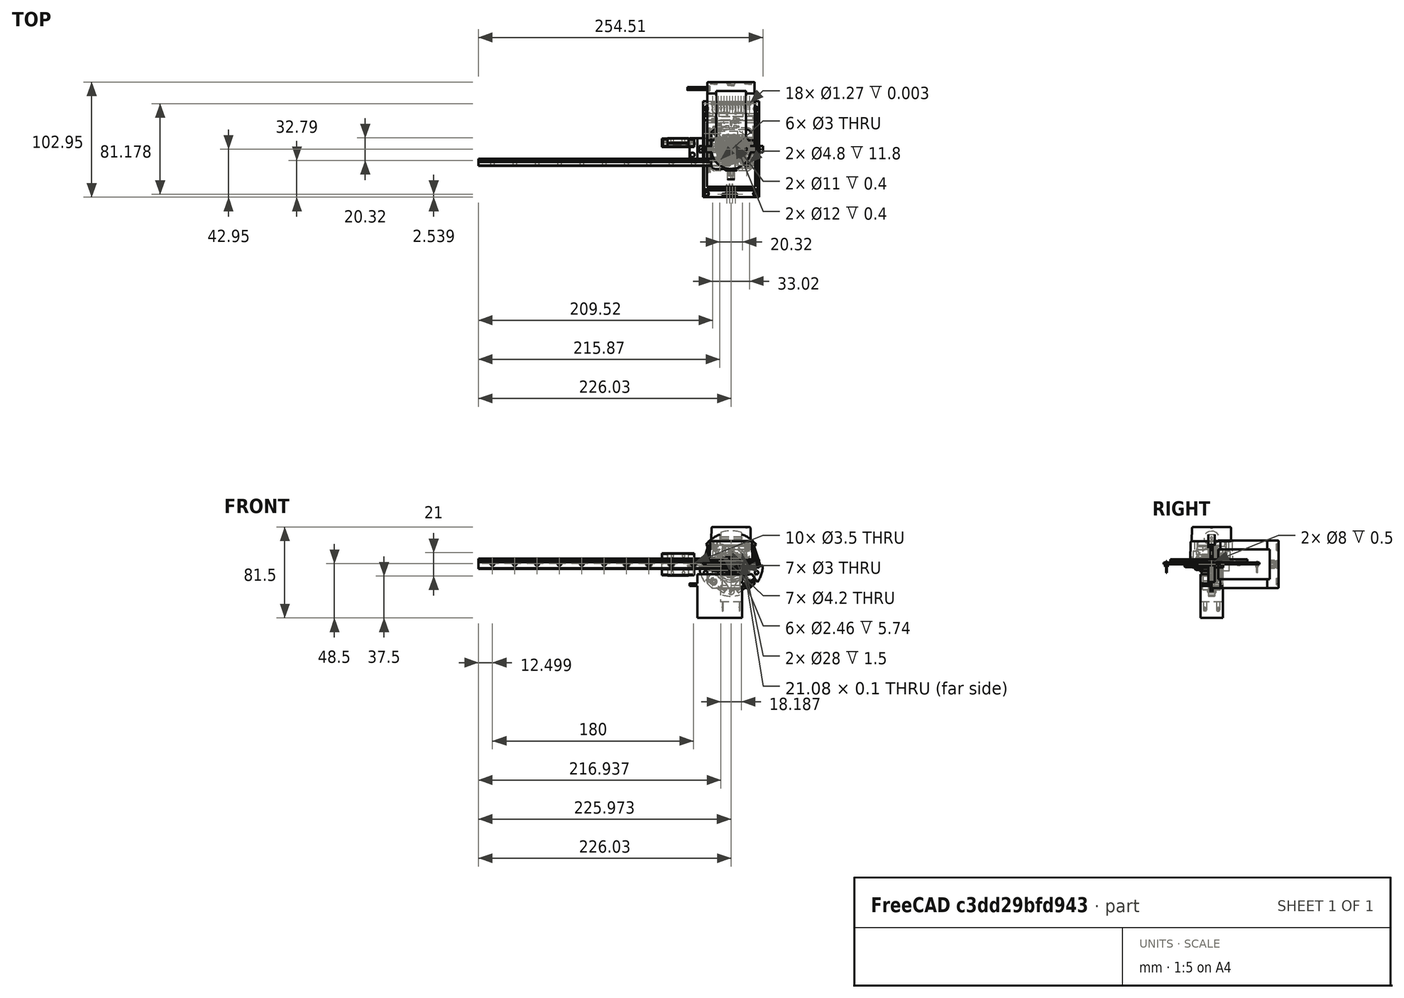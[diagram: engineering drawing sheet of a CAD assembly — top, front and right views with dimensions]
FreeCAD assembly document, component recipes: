
FREECAD ASSEMBLY — COMPONENT RECIPES ("generic-hardware")

This assembly document has 34 components, labeled P0..P33 below (a component is one placed body or linked part). 32 of them carry a construction recipe — the FreeCAD feature program that regenerates the part from scratch, quoted from this document or its linked companion documents; the rest are supplied as boundary geometry only. No exploded tour is included for this assembly.
NOTE — document 2 of 3 of this assembly tour. The two overview renders and the header above are repeated from document 1; the component sections below continue where the previous document stopped.
COMPONENT P17 — recipe-attached ("LD06", modeled in this document).
Construction recipe (the document's own serialized feature program — sketch geometry with constraints, then the solid features built on it; lengths are millimeters unless a unit is written):

FEATURE [Sketcher::SketchObject] Sketch189
  ArcFitTolerance = 0
  ExternalBSplineMaxDegree = 0
  ExternalBSplineTolerance = 0
  FixShape = 1
  FullyConstrained = true
  InternalTolerance = 1e-06
  InvalidShape = false
  MakeInternals = false
  MapMode = 5
  TreeRank = 0
  ValidateShape = false
  sketch-geometry (10):
    g0: ArcOfCircle CenterX=-14.1 CenterY=14.1 CenterZ=0 NormalX=0 NormalY=0 NormalZ=1 AngleXU=0 Radius=5.195 StartAngle=1.5708 EndAngle=3.14159
    g1: LineSegment StartX=-14.1 StartY=19.295 StartZ=0 EndX=14.1 EndY=19.295 EndZ=0
    g2: ArcOfCircle CenterX=14.1 CenterY=14.1 CenterZ=0 NormalX=0 NormalY=0 NormalZ=1 AngleXU=0 Radius=5.195 StartAngle=6.5809e-12 EndAngle=1.5708
    g3: LineSegment StartX=19.295 StartY=14.1 StartZ=0 EndX=19.295 EndY=-14.1 EndZ=0
    g4: ArcOfCircle CenterX=14.1 CenterY=-14.1 CenterZ=0 NormalX=0 NormalY=0 NormalZ=1 AngleXU=0 Radius=5.195 StartAngle=4.71239 EndAngle=6.28319
    g5: LineSegment StartX=14.1 StartY=-19.295 StartZ=0 EndX=-14.1 EndY=-19.295 EndZ=0
    g6: ArcOfCircle CenterX=-14.1 CenterY=-14.1 CenterZ=0 NormalX=0 NormalY=0 NormalZ=1 AngleXU=0 Radius=5.195 StartAngle=3.14159 EndAngle=4.71239
    g7: LineSegment StartX=-19.295 StartY=-14.1 StartZ=0 EndX=-19.295 EndY=14.1 EndZ=0
    g8: GeomPoint [constr] X=-19.295 Y=19.295 Z=0
    g9: GeomPoint [constr] X=19.295 Y=-19.295 Z=0
  constraints (23):
    c: Tangent(g0,g1) = 1.5708
    c: Tangent(g1,g2) = 1.5708
    c: Tangent(g2,g3) = 1.5708
    c: Tangent(g3,g4) = 1.5708
    c: Tangent(g4,g5) = 1.5708
    c: Tangent(g5,g6) = 1.5708
    c: Tangent(g6,g7) = 1.5708
    c: Tangent(g7,g0) = 1.5708
    c: Horizontal(g1)
    c: Horizontal(g5)
    c: Vertical(g3)
    c: Vertical(g7)
    c: Equal(g0,g2)
    c: Equal(g2,g4)
    c: Equal(g4,g6)
    c: PointOnObject(g8,g1)
    c: PointOnObject(g8,g7)
    c: PointOnObject(g9,g3)
    c: PointOnObject(g9,g5)
    c: Symmetric(g0,g4,g-1)
    c: Equal(g1,g3)
    c: DistanceY(g4,g1) = 38.59
    c: DistanceX(g0,g2) = 28.2
FEATURE [PartDesign::Pad] Pad077
  AddSubType = 0
  AlongSketchNormal = false
  AutoTaperInnerAngle = true
  CheckUpToFaceLimits = true
  ClaimChildren = false
  Direction = (0,0,1)
  Fit = 0
  FitJoin = 0
  FixShape = 1
  InnerFit = 0
  InnerFitJoin = 0
  InvalidShape = false
  Length = 20.7
  Length2 = 100
  NewSolid = false
  Profile = -> Sketch189
  Refine = true
  Suppress = false
  TaperAngle = -2
  TaperInnerAngle = 2
  TaperInnerAngleRev = 0
  TreeRank = 0
  Type = 0
  ValidateShape = true
  _ProfileBasedVersion = 0
FEATURE [Sketcher::SketchObject] Sketch190
  ArcFitTolerance = 0
  AttachmentSupport = -> [Pad077]
  ExternalBSplineMaxDegree = 0
  ExternalBSplineTolerance = 0
  FixShape = 1
  FullyConstrained = true
  InternalTolerance = 1e-06
  InvalidShape = false
  MakeInternals = false
  MapMode = 5
  Placement = pos=(0,0,20.7) rot=(0,0,1;0rad)
  Support = -> [Pad077]
  TreeRank = 0
  ValidateShape = false
  sketch-geometry (1):
    g0: Circle CenterX=0 CenterY=0 CenterZ=0 NormalX=0 NormalY=0 NormalZ=1 AngleXU=0 Radius=17.645
  constraints (2):
    c: Coincident(g0,g-1)
    c: Diameter(g0) = 35.29
FEATURE [PartDesign::Pad] Pad078
  AddSubType = 0
  AlongSketchNormal = false
  AutoTaperInnerAngle = true
  BaseFeature = -> Pad077
  CheckUpToFaceLimits = true
  ClaimChildren = false
  Direction = (0,0,1)
  Fit = 0
  FitJoin = 0
  FixShape = 1
  InnerFit = 0
  InnerFitJoin = 0
  InvalidShape = false
  Length = 12.8
  Length2 = 100
  NewSolid = false
  Profile = -> Sketch190
  Refine = true
  Suppress = false
  TaperAngle = -1.5
  TaperInnerAngle = 1.5
  TaperInnerAngleRev = 0
  TreeRank = 0
  Type = 0
  ValidateShape = true
  _ProfileBasedVersion = 0
FEATURE [Sketcher::SketchObject] Sketch191
  ArcFitTolerance = 0
  AttachmentOffset = pos=(0,0,17) rot=(0,0,1;0rad)
  ExternalBSplineMaxDegree = 0
  ExternalBSplineTolerance = 0
  FixShape = 1
  FullyConstrained = true
  InternalTolerance = 1e-06
  InvalidShape = false
  MakeInternals = false
  MapMode = 5
  Placement = pos=(0,-17,-4e-15) rot=(1,0,0;1.5708rad)
  TreeRank = 0
  ValidateShape = false
  sketch-geometry (5):
    g0: LineSegment StartX=-5 StartY=6.3 StartZ=0 EndX=-5 EndY=1.3 EndZ=0
    g1: LineSegment StartX=-5 StartY=1.3 StartZ=0 EndX=5 EndY=1.3 EndZ=0
    g2: LineSegment StartX=5 StartY=1.3 StartZ=0 EndX=5 EndY=6.3 EndZ=0
    g3: LineSegment StartX=5 StartY=6.3 StartZ=0 EndX=-5 EndY=6.3 EndZ=0
    g4: GeomPoint [constr] X=1.3758e-12 Y=3.8 Z=0
  constraints (13):
    c: Coincident(g0,g1)
    c: Coincident(g1,g2)
    c: Coincident(g2,g3)
    c: Coincident(g3,g0)
    c: Horizontal(g1)
    c: Horizontal(g3)
    c: Vertical(g0)
    c: Vertical(g2)
    c: Symmetric(g1,g0,g4)
    c: PointOnObject(g4,g-2)
    c: DistanceX(g3,g3) = 10
    c: DistanceY(g2,g2) = 5
    c: DistanceY(g-1,g4) = 3.8
FEATURE [PartDesign::Pocket] Pocket061
  AddSubType = 1
  AutoTaperInnerAngle = true
  BaseFeature = -> Pad078
  CheckUpToFaceLimits = true
  ClaimChildren = false
  Direction = (0,1,0)
  Fit = 0
  FitJoin = 0
  FixShape = 1
  InnerFit = 0
  InnerFitJoin = 0
  InvalidShape = false
  Length = 5
  Length2 = 100
  NewSolid = false
  Profile = -> Sketch191
  Refine = true
  Reversed = true
  Suppress = false
  TaperInnerAngle = 0
  TaperInnerAngleRev = 0
  TreeRank = 0
  Type = 1
  ValidateShape = true
  _ProfileBasedVersion = 0
  _Version = 0
FEATURE [Sketcher::SketchObject] Sketch192
  ArcFitTolerance = 0
  AttachmentSupport = -> [Pocket061]
  ExternalBSplineMaxDegree = 0
  ExternalBSplineTolerance = 0
  FixShape = 1
  FullyConstrained = false
  InternalTolerance = 1e-06
  InvalidShape = false
  MakeInternals = false
  MapMode = 5
  Placement = pos=(0,-17,0) rot=(1,0,0;1.5708rad)
  Support = -> [Pocket061]
  TreeRank = 0
  ValidateShape = false
  sketch-geometry (8):
    g0: Circle CenterX=-2.295 CenterY=3.8 CenterZ=0 NormalX=0 NormalY=0 NormalZ=1 AngleXU=0 Radius=0.765
    g1: Circle CenterX=-0.765 CenterY=3.8 CenterZ=0 NormalX=0 NormalY=0 NormalZ=1 AngleXU=0 Radius=0.765
    g2: Circle CenterX=0.765 CenterY=3.8 CenterZ=0 NormalX=0 NormalY=0 NormalZ=1 AngleXU=0 Radius=0.765
    g3: Circle CenterX=2.295 CenterY=3.8 CenterZ=0 NormalX=0 NormalY=0 NormalZ=1 AngleXU=0 Radius=0.765
    g4: LineSegment [constr] StartX=-2.295 StartY=3.8 StartZ=0 EndX=-0.765 EndY=3.8 EndZ=0
    g5: LineSegment [constr] StartX=-0.765 StartY=3.8 StartZ=0 EndX=0.765 EndY=3.8 EndZ=0
    g6: LineSegment [constr] StartX=0.765 StartY=3.8 StartZ=0 EndX=2.295 EndY=3.8 EndZ=0
    g7: GeomPoint [constr] X=1.8986e-12 Y=3.8 Z=0
  constraints (16):
    c: Horizontal(g3,g2)
    c: Symmetric(g1,g2,g-2)
    c: Symmetric(g0,g3,g-2)
    c: Coincident(g4,g0)
    c: Coincident(g4,g1)
    c: Coincident(g5,g1)
    c: Coincident(g5,g2)
    c: Coincident(g6,g2)
    c: Coincident(g6,g3)
    c: Equal(g6,g5)
    c: PointOnObject(g7,g5)
    c: Equal(g0,g1)
    c: Equal(g1,g2)
    c: Equal(g2,g3)
    c: Tangent(g3,g2)
    c: DistanceX(g4,g4) = 1.53
FEATURE [PartDesign::Pad] Pad079
  AddSubType = 0
  AlongSketchNormal = false
  AutoTaperInnerAngle = true
  BaseFeature = -> Pocket061
  CheckUpToFaceLimits = true
  ClaimChildren = false
  Direction = (0,-1,2e-16)
  Fit = 0
  FitJoin = 0
  FixShape = 1
  InnerFit = 0
  InnerFitJoin = 0
  InvalidShape = false
  Length = 10
  Length2 = 100
  NewSolid = false
  Profile = -> Sketch192
  Refine = true
  Suppress = false
  TaperInnerAngle = 0
  TaperInnerAngleRev = 0
  TreeRank = 0
  Type = 0
  ValidateShape = true
  _ProfileBasedVersion = 0
FEATURE [PartDesign::Fillet] Fillet045
  AddSubType = 0
  Base = -> Pad079 [Edge36]
  BaseFeature = -> Pad079
  FixShape = 1
  InvalidShape = false
  NewSolid = false
  Radius = 1
  Refine = true
  SupportTransform = false
  Suppress = false
  TreeRank = 0
  UseAllEdges = false
  ValidateShape = true
FEATURE [PartDesign::Fillet] Fillet046
  AddSubType = 0
  Base = -> Fillet045 [Edge13]
  BaseFeature = -> Fillet045
  FixShape = 1
  InvalidShape = false
  NewSolid = false
  Radius = 1
  Refine = true
  SupportTransform = false
  Suppress = false
  TreeRank = 0
  UseAllEdges = false
  ValidateShape = true
FEATURE [Sketcher::SketchObject] Sketch193
  ArcFitTolerance = 0
  AttachmentSupport = -> [Fillet046]
  ExternalBSplineMaxDegree = 0
  ExternalBSplineTolerance = 0
  FixShape = 1
  FullyConstrained = true
  InternalTolerance = 1e-06
  InvalidShape = false
  MakeInternals = false
  MapMode = 5
  Placement = pos=(0,0,33.5) rot=(0,0,1;0rad)
  Support = -> [Fillet046]
  TreeRank = 0
  ValidateShape = false
  sketch-geometry (3):
    g0: LineSegment StartX=13 StartY=-0.866025 StartZ=0 EndX=13 EndY=0.866025 EndZ=0
    g1: LineSegment StartX=13 StartY=0.866025 StartZ=0 EndX=14.5 EndY=-2.501e-11 EndZ=0
    g2: LineSegment StartX=14.5 StartY=-2.501e-11 StartZ=0 EndX=13 EndY=-0.866025 EndZ=0
  constraints (9):
    c: Vertical(g0)
    c: Coincident(g0,g1)
    c: PointOnObject(g1,g-1)
    c: Coincident(g1,g2)
    c: Coincident(g2,g0)
    c: Equal(g2,g1)
    c: Equal(g1,g0)
    c: DistanceX(g-1,g0) = 13
    c: DistanceX(g0,g1) = 1.5
FEATURE [PartDesign::Pocket] Pocket062
  AddSubType = 1
  AutoTaperInnerAngle = true
  BaseFeature = -> Fillet046
  CheckUpToFaceLimits = true
  ClaimChildren = false
  Direction = (0,0,-1)
  Fit = 0
  FitJoin = 0
  FixShape = 1
  InnerFit = 0
  InnerFitJoin = 0
  InvalidShape = false
  Length = 1
  Length2 = 100
  NewSolid = false
  Profile = -> Sketch193
  Refine = true
  Suppress = false
  TaperInnerAngle = 0
  TaperInnerAngleRev = 0
  TreeRank = 0
  Type = 0
  ValidateShape = true
  _ProfileBasedVersion = 0
  _Version = 0
FEATURE [Sketcher::SketchObject] Sketch194
  ArcFitTolerance = 0
  AttachmentSupport = -> [Pocket062]
  ExternalBSplineMaxDegree = 0
  ExternalBSplineTolerance = 0
  FixShape = 1
  FullyConstrained = true
  InternalTolerance = 1e-06
  InvalidShape = false
  MakeInternals = false
  MapMode = 5
  Placement = pos=(0,0,0) rot=(0,0,1;3.14159rad)
  Support = -> [Pocket062]
  TreeRank = 0
  ValidateShape = false
  sketch-geometry (4):
    g0: Circle [constr] CenterX=-14.1 CenterY=14.1 CenterZ=0 NormalX=0 NormalY=0 NormalZ=1 AngleXU=0 Radius=2.4
    g1: Circle [constr] CenterX=14.1 CenterY=-14.1 CenterZ=0 NormalX=0 NormalY=0 NormalZ=1 AngleXU=0 Radius=2.4
    g2: Circle CenterX=-14.1 CenterY=14.1 CenterZ=0 NormalX=0 NormalY=0 NormalZ=1 AngleXU=0 Radius=1.225
    g3: Circle CenterX=14.1 CenterY=-14.1 CenterZ=0 NormalX=0 NormalY=0 NormalZ=1 AngleXU=0 Radius=1.225
  constraints (9):
    c: Symmetric(g0,g1,g-1)
    c: Equal(g0,g1)
    c: Diameter(g0) = 4.8
    c: DistanceX(g0,g-1) = 14.1
    c: DistanceY(g-1,g0) = 14.1
    c: Coincident(g2,g0)
    c: Coincident(g3,g1)
    c: Equal(g3,g2)
    c: Diameter(g3) = 2.45
FEATURE [Sketcher::SketchObject] Sketch195
  ArcFitTolerance = 0
  AttachmentOffset = pos=(0,0,21.7) rot=(0,0,1;0rad)
  ExternalBSplineMaxDegree = 0
  ExternalBSplineTolerance = 0
  FixShape = 1
  FullyConstrained = true
  InternalTolerance = 1e-06
  InvalidShape = false
  MakeInternals = false
  MapMode = 5
  Placement = pos=(0,0,21.7) rot=(0,0,1;0rad)
  TreeRank = 0
  ValidateShape = false
  sketch-geometry (2):
    g0: Circle CenterX=0 CenterY=0 CenterZ=0 NormalX=0 NormalY=0 NormalZ=1 AngleXU=0 Radius=20
    g1: Circle CenterX=0 CenterY=0 CenterZ=0 NormalX=0 NormalY=0 NormalZ=1 AngleXU=0 Radius=500
  constraints (4):
    c: Coincident(g0,g-1)
    c: Coincident(g1,g0)
    c: Diameter(g1) = 1000
    c: Diameter(g0) = 40
FEATURE [PartDesign::Pad] Pad013
  AddSubType = 0
  AlongSketchNormal = false
  AutoTaperInnerAngle = true
  CheckUpToFaceLimits = true
  ClaimChildren = false
  Direction = (0,0,1)
  Fit = 0
  FitJoin = 0
  FixShape = 1
  InnerFit = 0
  InnerFitJoin = 0
  InvalidShape = false
  Length = 10
  Length2 = 100
  NewSolid = false
  Placement = pos=(0,0,21.7) rot=(0,0,1;0rad)
  Profile = -> Sketch195
  Refine = true
  Suppress = false
  TaperInnerAngle = 0
  TaperInnerAngleRev = 0
  TreeRank = 0
  Type = 0
  ValidateShape = true
  _ProfileBasedVersion = 0
FEATURE [PartDesign::Body] Body091  label="OpticalWindow"
  AutoGroupSolids = false
  ClaimAllChildren = false
  ExportMode = 0
  FixShape = 1
  Group = -> [Sketch195,Pad013]
  InvalidShape = false
  Origin = -> Origin182
  SingleSolid = true
  Tip = -> Pad013
  TreeRank = 0
  ValidateShape = false
  _ExportChildren = -> [Pad013]
  _GroupVersion = 1
FEATURE [PartDesign::Pocket] Pocket076
  AddSubType = 1
  AutoTaperInnerAngle = true
  BaseFeature = -> Pocket062
  CheckUpToFaceLimits = true
  ClaimChildren = false
  Direction = (0,0,-1)
  Fit = 0
  FitJoin = 0
  FixShape = 1
  InnerFit = 0
  InnerFitJoin = 0
  InvalidShape = false
  Length = 5
  Length2 = 5
  NewSolid = false
  Profile = -> Sketch194
  ReferenceAxis = -> Sketch194 [N_Axis]
  Refine = true
  Reversed = true
  Suppress = false
  TaperInnerAngle = 0
  TaperInnerAngleRev = 0
  TreeRank = 0
  Type = 1
  ValidateShape = true
  _ProfileBasedVersion = 0
  _Version = 0
FEATURE [Sketcher::SketchObject] Sketch237
  ArcFitTolerance = 0
  AttachmentSupport = -> [Pocket076]
  ExternalBSplineMaxDegree = 0
  ExternalBSplineTolerance = 0
  ExternalGeometry = -> [Pocket076]
  FixShape = 1
  FullyConstrained = true
  InternalTolerance = 1e-06
  InvalidShape = false
  MakeInternals = false
  MapMode = 5
  Placement = pos=(0,0,0) rot=(1,0,0;3.14159rad)
  Support = -> [Pocket076]
  TreeRank = 0
  ValidateShape = false
  sketch-geometry (2):
    g0: Circle CenterX=14.1 CenterY=14.1 CenterZ=0 NormalX=0 NormalY=0 NormalZ=1 AngleXU=0 Radius=2.4
    g1: Circle CenterX=-14.1 CenterY=-14.1 CenterZ=0 NormalX=0 NormalY=0 NormalZ=1 AngleXU=0 Radius=2.4
  constraints (4):
    c: Coincident(g0,g-3)
    c: Coincident(g1,g-4)
    c: Equal(g0,g1)
    c: Diameter(g0) = 4.8
FEATURE [PartDesign::Pocket] Pocket077
  AddSubType = 1
  AutoTaperInnerAngle = true
  BaseFeature = -> Pocket076
  CheckUpToFaceLimits = true
  ClaimChildren = false
  Direction = (0,0,1)
  Fit = 0
  FitJoin = 0
  FixShape = 1
  InnerFit = 0
  InnerFitJoin = 0
  InvalidShape = false
  Length = 11.8
  Length2 = 5
  NewSolid = false
  Profile = -> Sketch237
  ReferenceAxis = -> Sketch237 [N_Axis]
  Refine = true
  Suppress = false
  TaperInnerAngle = 0
  TaperInnerAngleRev = 0
  TreeRank = 0
  Type = 0
  ValidateShape = true
  _ProfileBasedVersion = 0
  _Version = 0
FEATURE [PartDesign::Body] Body090  label="BaseLD06"
  AutoGroupSolids = false
  ClaimAllChildren = false
  ExportMode = 0
  FixShape = 1
  Group = -> [Sketch189,Pad077,Sketch190,Pad078,Sketch191,Pocket061,Sketch192,Pad079,Fillet045,Fillet046,Sketch193,Pocket062,Sketch194,Pocket076,Sketch237,Pocket077]
  InvalidShape = false
  Origin = -> Origin181
  SingleSolid = true
  Tip = -> Pocket077
  TreeRank = 0
  ValidateShape = false
  _ExportChildren = -> [Pad077,Pad078,Pocket061,Pad079,Fillet045,Fillet046,Pocket062,Pocket076,Pocket077]
  _GroupVersion = 1
COMPONENT P18 — recipe-attached ("MG996", modeled in this document).
Construction recipe (the document's own serialized feature program — sketch geometry with constraints, then the solid features built on it; lengths are millimeters unless a unit is written):

FEATURE [Sketcher::SketchObject] Sketch086
  ArcFitTolerance = 0
  ExternalBSplineMaxDegree = 0
  ExternalBSplineTolerance = 0
  FixShape = 1
  FullyConstrained = true
  InternalTolerance = 1e-06
  InvalidShape = false
  MakeInternals = false
  MapMode = 5
  Placement = pos=(0,0,0) rot=(1,0,0;1.5708rad)
  TreeRank = 0
  ValidateShape = false
  sketch-geometry (12):
    g0: LineSegment StartX=-37 StartY=-18.5 StartZ=0 EndX=-37 EndY=-16 EndZ=0
    g1: LineSegment StartX=-37 StartY=-16 StartZ=0 EndX=-30 EndY=-16 EndZ=0
    g2: LineSegment StartX=-30 StartY=-16 StartZ=0 EndX=-30 EndY=-8 EndZ=0
    g3: LineSegment StartX=-30 StartY=-8 StartZ=0 EndX=10 EndY=-8 EndZ=0
    g4: LineSegment StartX=10 StartY=-8 StartZ=0 EndX=10 EndY=-16 EndZ=0
    g5: LineSegment StartX=10 StartY=-16 StartZ=0 EndX=17 EndY=-16 EndZ=0
    g6: LineSegment StartX=17 StartY=-16 StartZ=0 EndX=17 EndY=-18.5 EndZ=0
    g7: LineSegment StartX=17 StartY=-18.5 StartZ=0 EndX=10 EndY=-18.5 EndZ=0
    g8: LineSegment StartX=10 StartY=-18.5 StartZ=0 EndX=10 EndY=-47 EndZ=0
    g9: LineSegment StartX=10 StartY=-47 StartZ=0 EndX=-30 EndY=-47 EndZ=0
    g10: LineSegment StartX=-30 StartY=-47 StartZ=0 EndX=-30 EndY=-18.5 EndZ=0
    g11: LineSegment StartX=-30 StartY=-18.5 StartZ=0 EndX=-37 EndY=-18.5 EndZ=0
  constraints (33):
    c: Vertical(g0)
    c: Coincident(g0,g1)
    c: Horizontal(g1)
    c: Coincident(g1,g2)
    c: Vertical(g2)
    c: Coincident(g2,g3)
    c: Horizontal(g3)
    c: Coincident(g3,g4)
    c: Coincident(g4,g5)
    c: Coincident(g5,g6)
    c: Vertical(g6)
    c: Coincident(g6,g7)
    c: Horizontal(g7)
    c: Coincident(g7,g8)
    c: Vertical(g8)
    c: Coincident(g8,g9)
    c: Horizontal(g9)
    c: Coincident(g9,g10)
    c: Coincident(g10,g11)
    c: Coincident(g11,g0)
    c: Horizontal(g11)
    c: Tangent(g4,g8) = -1.5708
    c: Tangent(g10,g2)
    c: Equal(g1,g5)
    c: Tangent(g1,g5)
    c: Equal(g6,g0)
    c: DistanceX(g-1,g3) = 10
    c: DistanceX(g0,g5) = 54
    c: DistanceX(g10,g7) = 40
    c: DistanceY(g9,g-1) = 47
    c: DistanceY(g3,g-1) = 8
    c: DistanceY(g6,g6) = 2.5
    c: DistanceY(g0,g-1) = 18.5
FEATURE [PartDesign::Pad] Pad050
  AddSubType = 0
  AutoTaperInnerAngle = true
  CheckUpToFaceLimits = true
  ClaimChildren = false
  Direction = (0,-1,0)
  Fit = 0
  FitJoin = 0
  FixShape = 1
  InnerFit = 0
  InnerFitJoin = 0
  InvalidShape = false
  Length = 20
  Length2 = 100
  Midplane = true
  NewSolid = false
  Placement = pos=(0,0,0) rot=(1,0,0;1.5708rad)
  Profile = -> Sketch086
  Refine = true
  Suppress = false
  TaperInnerAngle = 0
  TaperInnerAngleRev = 0
  TreeRank = 0
  Type = 0
  ValidateShape = true
  _ProfileBasedVersion = 0
FEATURE [Sketcher::SketchObject] Sketch087
  ArcFitTolerance = 0
  ExternalBSplineMaxDegree = 0
  ExternalBSplineTolerance = 0
  FixShape = 1
  FullyConstrained = true
  InternalTolerance = 1e-06
  InvalidShape = false
  MakeInternals = false
  MapMode = 5
  TreeRank = 0
  ValidateShape = false
  sketch-geometry (4):
    g0: Circle CenterX=14.5 CenterY=5 CenterZ=0 NormalX=0 NormalY=0 NormalZ=1 AngleXU=0 Radius=2
    g1: Circle CenterX=14.5 CenterY=-5 CenterZ=0 NormalX=0 NormalY=0 NormalZ=1 AngleXU=0 Radius=2
    g2: Circle CenterX=-34.5 CenterY=5 CenterZ=0 NormalX=0 NormalY=0 NormalZ=1 AngleXU=0 Radius=2
    g3: Circle CenterX=-34.5 CenterY=-5 CenterZ=0 NormalX=0 NormalY=0 NormalZ=1 AngleXU=0 Radius=2
  constraints (10):
    c: Equal(g2,g3)
    c: Equal(g3,g1)
    c: Equal(g1,g0)
    c: Symmetric(g0,g1,g-1)
    c: Symmetric(g2,g3,g-1)
    c: Horizontal(g2,g0)
    c: Diameter(g0) = 4
    c: DistanceY(g1,g0) = 10
    c: DistanceX(g2,g0) = 49
    c: DistanceX(g-1,g0) = 14.5
FEATURE [PartDesign::Pocket] Pocket033
  AddSubType = 1
  AutoTaperInnerAngle = true
  BaseFeature = -> Pad050
  CheckUpToFaceLimits = true
  ClaimChildren = false
  Direction = (0,0,-1)
  Fit = 0
  FitJoin = 0
  FixShape = 1
  InnerFit = 0
  InnerFitJoin = 0
  InvalidShape = false
  Length = 5
  Length2 = 100
  NewSolid = false
  Placement = pos=(0,0,0) rot=(1,0,0;1.5708rad)
  Profile = -> Sketch087
  Refine = true
  Suppress = false
  TaperInnerAngle = 0
  TaperInnerAngleRev = 0
  TreeRank = 0
  Type = 1
  ValidateShape = true
  _ProfileBasedVersion = 0
  _Version = 0
FEATURE [PartDesign::Fillet] Fillet024
  AddSubType = 0
  Base = -> Pocket033 [Edge28,Edge19,Edge4,Edge3]
  BaseFeature = -> Pocket033
  FixShape = 1
  InvalidShape = false
  NewSolid = false
  Placement = pos=(0,0,0) rot=(1,0,0;1.5708rad)
  Radius = 1
  Refine = true
  SupportTransform = false
  Suppress = false
  TreeRank = 0
  UseAllEdges = false
  ValidateShape = true
FEATURE [Sketcher::SketchObject] Sketch090
  ArcFitTolerance = 0
  AttachmentOffset = pos=(0,0,-2) rot=(0,0,1;0rad)
  ExternalBSplineMaxDegree = 0
  ExternalBSplineTolerance = 0
  FixShape = 1
  FullyConstrained = true
  InternalTolerance = 1e-06
  InvalidShape = false
  MakeInternals = false
  MapMode = 5
  Placement = pos=(0,0,-2) rot=(0,0,1;0rad)
  TreeRank = 0
  ValidateShape = false
  sketch-geometry (1):
    g0: Circle CenterX=0 CenterY=0 CenterZ=0 NormalX=0 NormalY=0 NormalZ=1 AngleXU=0 Radius=3
  constraints (2):
    c: Coincident(g0,g-1)
    c: Diameter(g0) = 6
FEATURE [PartDesign::Pad] Pad053
  AddSubType = 0
  AutoTaperInnerAngle = true
  CheckUpToFaceLimits = true
  ClaimChildren = false
  Direction = (0,0,1)
  Fit = 0
  FitJoin = 0
  FixShape = 1
  InnerFit = 0
  InnerFitJoin = 0
  InvalidShape = false
  Length = 10
  Length2 = 100
  NewSolid = false
  Placement = pos=(0,0,-2) rot=(0,0,1;0rad)
  Profile = -> Sketch090
  Refine = true
  Reversed = true
  Suppress = false
  TaperInnerAngle = 0
  TaperInnerAngleRev = 0
  TreeRank = 0
  Type = 0
  ValidateShape = true
  _ProfileBasedVersion = 0
FEATURE [PartDesign::Chamfer] Chamfer029
  AddSubType = 0
  Angle = 45
  Base = -> Pad053 [Edge2]
  BaseFeature = -> Pad053
  ChamferType = 0
  FixShape = 1
  FlipDirection = false
  InvalidShape = false
  NewSolid = false
  Placement = pos=(0,0,-2) rot=(0,0,1;0rad)
  Refine = true
  Size = 0.5
  Size2 = 1
  SupportTransform = false
  Suppress = false
  TreeRank = 0
  UseAllEdges = false
  ValidateShape = true
FEATURE [PartDesign::Body] Body043  label="ServoAxis001"
  AutoGroupSolids = false
  ClaimAllChildren = false
  ExportMode = 0
  FixShape = 1
  Group = -> [Sketch090,Pad053,Chamfer029]
  InvalidShape = false
  Origin = -> Origin064
  SingleSolid = true
  Tip = -> Chamfer029
  TreeRank = 0
  ValidateShape = false
  _ExportChildren = -> [Pad053,Chamfer029]
  _GroupVersion = 1
FEATURE [Sketcher::SketchObject] Sketch235
  ArcFitTolerance = 0
  AttachmentSupport = -> [Fillet024]
  ExternalBSplineMaxDegree = 0
  ExternalBSplineTolerance = 0
  FixShape = 1
  FullyConstrained = true
  InternalTolerance = 1e-06
  InvalidShape = false
  MakeInternals = false
  MapMode = 5
  Placement = pos=(0,5.3e-15,-8) rot=(0,0,1;3.14159rad)
  Support = -> [Fillet024]
  TreeRank = 0
  ValidateShape = false
  sketch-geometry (1):
    g0: Circle CenterX=0 CenterY=0 CenterZ=0 NormalX=0 NormalY=0 NormalZ=1 AngleXU=0 Radius=6.5
  constraints (2):
    c: Coincident(g0,g-1)
    c: Diameter(g0) = 13
FEATURE [PartDesign::Pad] Pad096
  AddSubType = 0
  AutoTaperInnerAngle = true
  BaseFeature = -> Fillet024
  CheckUpToFaceLimits = true
  ClaimChildren = false
  Direction = (0,-7e-16,1)
  Fit = 0
  FitJoin = 0
  FixShape = 1
  InnerFit = 0
  InnerFitJoin = 0
  InvalidShape = false
  Length = 2
  Length2 = 10
  NewSolid = false
  Placement = pos=(0,0,0) rot=(1,0,0;1.5708rad)
  Profile = -> Sketch235
  ReferenceAxis = -> Sketch235 [N_Axis]
  Refine = true
  Suppress = false
  TaperInnerAngle = 0
  TaperInnerAngleRev = 0
  TreeRank = 0
  Type = 0
  ValidateShape = true
  _ProfileBasedVersion = 0
FEATURE [PartDesign::Fillet] Fillet
  AddSubType = 0
  Base = -> Pad096 [Edge61]
  BaseFeature = -> Pad096
  FixShape = 1
  InvalidShape = false
  NewSolid = false
  Placement = pos=(0,0,0) rot=(1,0,0;1.5708rad)
  Radius = 1
  Refine = true
  SupportTransform = false
  Suppress = false
  TreeRank = 0
  UseAllEdges = false
  ValidateShape = true
FEATURE [PartDesign::Body] Body041  label="ServoBody001"
  AutoGroupSolids = false
  ClaimAllChildren = false
  ExportMode = 0
  FixShape = 1
  Group = -> [Sketch086,Pad050,Sketch087,Pocket033,Fillet024,Sketch235,Pad096,Fillet]
  InvalidShape = false
  Origin = -> Origin062
  Placement = pos=(0,0,-1) rot=(0,0,1;0rad)
  SingleSolid = true
  Tip = -> Fillet
  TreeRank = 0
  ValidateShape = false
  _ExportChildren = -> [Pad050,Pocket033,Fillet024,Pad096,Fillet]
  _GroupVersion = 1
COMPONENT P19 — recipe-attached ("OmniPancake", modeled in this document).
Construction recipe (the document's own serialized feature program — sketch geometry with constraints, then the solid features built on it; lengths are millimeters unless a unit is written):

FEATURE [Sketcher::SketchObject] Sketch095
  ArcFitTolerance = 0
  ExternalBSplineMaxDegree = 0
  ExternalBSplineTolerance = 0
  FixShape = 1
  FullyConstrained = true
  InternalTolerance = 1e-06
  InvalidShape = false
  MakeInternals = false
  MapMode = 5
  Placement = pos=(0,0,0) rot=(1,0,0;1.5708rad)
  TreeRank = 0
  ValidateShape = false
  sketch-geometry (2):
    g0: Circle CenterX=0 CenterY=0 CenterZ=0 NormalX=0 NormalY=0 NormalZ=1 AngleXU=0 Radius=14
    g1: Circle CenterX=0 CenterY=0 CenterZ=0 NormalX=0 NormalY=0 NormalZ=1 AngleXU=0 Radius=28.5
  constraints (4):
    c: Coincident(g0,g-1)
    c: Diameter(g0) = 28
    c: Coincident(g1,g0)
    c: Diameter(g1) = 57
FEATURE [PartDesign::Pad] Pad057
  AddSubType = 0
  AutoTaperInnerAngle = true
  CheckUpToFaceLimits = true
  ClaimChildren = false
  Direction = (0,-1,0)
  Fit = 0
  FitJoin = 0
  FixShape = 1
  InnerFit = 0
  InnerFitJoin = 0
  InvalidShape = false
  Length = 5.5
  Length2 = 100
  Midplane = true
  NewSolid = false
  Placement = pos=(0,0,0) rot=(1,0,0;1.5708rad)
  Profile = -> Sketch095
  Refine = true
  Suppress = false
  TaperInnerAngle = 0
  TaperInnerAngleRev = 0
  TreeRank = 0
  Type = 0
  ValidateShape = true
  _ProfileBasedVersion = 0
FEATURE [Sketcher::SketchObject] Sketch096
  ArcFitTolerance = 0
  AttachmentSupport = -> [XZ_Plane057]
  ExternalBSplineMaxDegree = 0
  ExternalBSplineTolerance = 0
  FixShape = 1
  FullyConstrained = true
  InternalTolerance = 1e-06
  InvalidShape = false
  MakeInternals = false
  MapMode = 5
  Placement = pos=(0,0,0) rot=(1,0,0;1.5708rad)
  TreeRank = 0
  ValidateShape = false
  sketch-geometry (2):
    g0: Circle CenterX=0 CenterY=0 CenterZ=0 NormalX=0 NormalY=0 NormalZ=1 AngleXU=0 Radius=6
    g1: Circle CenterX=0 CenterY=0 CenterZ=0 NormalX=0 NormalY=0 NormalZ=1 AngleXU=0 Radius=14
  constraints (4):
    c: Coincident(g0,g-1)
    c: Diameter(g0) = 12
    c: Coincident(g1,g0)
    c: Diameter(g1) = 28
FEATURE [PartDesign::Pad] Pad058
  AddSubType = 0
  AutoTaperInnerAngle = true
  BaseFeature = -> Pad057
  CheckUpToFaceLimits = true
  ClaimChildren = false
  Direction = (0,-1,-2e-16)
  Fit = 0
  FitJoin = 0
  FixShape = 1
  InnerFit = 0
  InnerFitJoin = 0
  InvalidShape = false
  Length = 2.5
  Length2 = 100
  Midplane = true
  NewSolid = false
  Placement = pos=(0,0,0) rot=(1,0,0;1.5708rad)
  Profile = -> Sketch096
  Refine = true
  Suppress = false
  TaperInnerAngle = 0
  TaperInnerAngleRev = 0
  TreeRank = 0
  Type = 0
  ValidateShape = true
  _ProfileBasedVersion = 0
FEATURE [Sketcher::SketchObject] Sketch097
  ArcFitTolerance = 0
  ExternalBSplineMaxDegree = 0
  ExternalBSplineTolerance = 0
  FixShape = 1
  FullyConstrained = false
  InternalTolerance = 1e-06
  InvalidShape = false
  MakeInternals = false
  MapMode = 5
  Placement = pos=(0,0,0) rot=(1,0,0;1.5708rad)
  TreeRank = 0
  ValidateShape = false
  sketch-geometry (6):
    g0: LineSegment StartX=-9.7 StartY=26.7985 StartZ=0 EndX=-9.7 EndY=17.7985 EndZ=0
    g1: LineSegment StartX=9.7 StartY=26.7985 StartZ=0 EndX=9.7 EndY=17.7985 EndZ=0
    g2: ArcOfCircle CenterX=-1.9e-15 CenterY=37.1169 CenterZ=0 NormalX=0 NormalY=0 NormalZ=1 AngleXU=0 Radius=21.6169 StartAngle=4.24705 EndAngle=5.17773
    g3: GeomPoint [constr] X=0 Y=15.5 Z=0
    g4: ArcOfCircle CenterX=0 CenterY=0 CenterZ=0 NormalX=0 NormalY=0 NormalZ=1 AngleXU=0 Radius=28.5 StartAngle=1.22351 EndAngle=1.91809
    g5: Circle [constr] CenterX=0 CenterY=0 CenterZ=0 NormalX=0 NormalY=0 NormalZ=1 AngleXU=0 Radius=28.5
  constraints (16):
    c: Vertical(g0)
    c: Vertical(g1)
    c: Symmetric(g1,g0,g-2)
    c: Equal(g0,g1)
    c: Coincident(g2,g0)
    c: Coincident(g2,g1)
    c: PointOnObject(g3,g2)
    c: PointOnObject(g3,g-2)
    c: DistanceY(g-1,g3) = 15.5
    c: DistanceY(g1,g1) = 9
    c: Coincident(g4,g-1)
    c: Coincident(g4,g0)
    c: DistanceX(g0,g1) = 19.4
    c: Coincident(g5,g4)
    c: PointOnObject(g1,g5)
    c: Diameter(g5) = 57
FEATURE [PartDesign::Pocket] Pocket036
  AddSubType = 1
  AutoTaperInnerAngle = true
  BaseFeature = -> Pad058
  CheckUpToFaceLimits = true
  ClaimChildren = false
  Direction = (0,1,0)
  Fit = 0
  FitJoin = 0
  FixShape = 1
  InnerFit = 0
  InnerFitJoin = 0
  InvalidShape = false
  Length = 5
  Length2 = 100
  Midplane = true
  NewSolid = false
  Placement = pos=(0,0,0) rot=(1,0,0;1.5708rad)
  Profile = -> Sketch097
  Refine = true
  Suppress = false
  TaperInnerAngle = 0
  TaperInnerAngleRev = 0
  TreeRank = 0
  Type = 1
  ValidateShape = true
  _ProfileBasedVersion = 0
  _Version = 0
FEATURE [PartDesign::PolarPattern] PolarPattern017
  AddSubType = 0
  Angle = 360
  Axis = -> Sketch097 [N_Axis]
  BaseFeature = -> Pocket036
  CopyShape = true
  FixShape = 1
  InvalidShape = false
  NewSolid = false
  Occurrences = 5
  OriginalSubs = -> [Pocket036]
  Originals = -> [Pocket036]
  ParallelTransform = true
  Placement = pos=(0,0,0) rot=(1,0,0;1.5708rad)
  Refine = true
  SubTransform = true
  Suppress = false
  TreeRank = 0
  ValidateShape = true
  _Version = 0
FEATURE [Sketcher::SketchObject] Sketch098
  ArcFitTolerance = 0
  ExternalBSplineMaxDegree = 0
  ExternalBSplineTolerance = 0
  FixShape = 1
  FullyConstrained = true
  InternalTolerance = 1e-06
  InvalidShape = false
  MakeInternals = false
  MapMode = 5
  Placement = pos=(0,0,0) rot=(0.57735,0.57735,0.57735;2.0944rad)
  TreeRank = 0
  ValidateShape = false
  sketch-geometry (3):
    g0: Circle CenterX=0 CenterY=23.5 CenterZ=0 NormalX=0 NormalY=0 NormalZ=1 AngleXU=0 Radius=1
    g1: Circle [constr] CenterX=0 CenterY=23.5 CenterZ=0 NormalX=0 NormalY=0 NormalZ=1 AngleXU=0 Radius=6.5
    g2: GeomPoint [constr] X=0 Y=30 Z=0
  constraints (7):
    c: PointOnObject(g0,g-2)
    c: Diameter(g0) = 2
    c: Coincident(g1,g0)
    c: Diameter(g1) = 13
    c: PointOnObject(g2,g1)
    c: PointOnObject(g2,g-2)
    c: DistanceY(g2) = 30
FEATURE [PartDesign::Pad] Pad059
  AddSubType = 0
  AutoTaperInnerAngle = true
  BaseFeature = -> PolarPattern017
  CheckUpToFaceLimits = true
  ClaimChildren = false
  Direction = (1,1e-16,-1e-16)
  Fit = 0
  FitJoin = 0
  FixShape = 1
  InnerFit = 0
  InnerFitJoin = 0
  InvalidShape = false
  Length = 20
  Length2 = 100
  Midplane = true
  NewSolid = false
  Placement = pos=(0,0,0) rot=(1,0,0;1.5708rad)
  Profile = -> Sketch098
  Refine = true
  Suppress = false
  TaperInnerAngle = 0
  TaperInnerAngleRev = 0
  TreeRank = 0
  Type = 0
  ValidateShape = true
  _ProfileBasedVersion = 0
FEATURE [PartDesign::PolarPattern] PolarPattern018
  AddSubType = 0
  Angle = 360
  Axis = -> Y_Axis057
  BaseFeature = -> Pad059
  CopyShape = true
  FixShape = 1
  InvalidShape = false
  NewSolid = false
  Occurrences = 5
  OriginalSubs = -> [Pad059]
  Originals = -> [Pad059]
  ParallelTransform = true
  Placement = pos=(0,0,0) rot=(1,0,0;1.5708rad)
  Refine = true
  SubTransform = true
  Suppress = false
  TreeRank = 0
  ValidateShape = true
  _Version = 0
FEATURE [Sketcher::SketchObject] Sketch099
  ArcFitTolerance = 0
  ExternalBSplineMaxDegree = 0
  ExternalBSplineTolerance = 0
  FixShape = 1
  FullyConstrained = true
  InternalTolerance = 1e-06
  InvalidShape = false
  MakeInternals = false
  MapMode = 5
  Placement = pos=(0,0,0) rot=(1,0,0;1.5708rad)
  TreeRank = 0
  ValidateShape = false
  sketch-geometry (1):
    g0: Circle CenterX=0 CenterY=10.5 CenterZ=0 NormalX=0 NormalY=0 NormalZ=1 AngleXU=0 Radius=1.5
  constraints (3):
    c: PointOnObject(g0,g-2)
    c: Diameter(g0) = 3
    c: DistanceY(g0) = 10.5
FEATURE [PartDesign::Pocket] Pocket037
  AddSubType = 1
  AutoTaperInnerAngle = true
  BaseFeature = -> PolarPattern018
  CheckUpToFaceLimits = true
  ClaimChildren = false
  Direction = (0,1,0)
  Fit = 0
  FitJoin = 0
  FixShape = 1
  InnerFit = 0
  InnerFitJoin = 0
  InvalidShape = false
  Length = 5
  Length2 = 100
  Midplane = true
  NewSolid = false
  Placement = pos=(0,0,0) rot=(1,0,0;1.5708rad)
  Profile = -> Sketch099
  Refine = true
  Suppress = false
  TaperInnerAngle = 0
  TaperInnerAngleRev = 0
  TreeRank = 0
  Type = 1
  ValidateShape = true
  _ProfileBasedVersion = 0
  _Version = 0
FEATURE [PartDesign::PolarPattern] PolarPattern019
  AddSubType = 0
  Angle = 360
  Axis = -> Y_Axis057
  BaseFeature = -> Pocket037
  CopyShape = true
  FixShape = 1
  InvalidShape = false
  NewSolid = false
  Occurrences = 6
  OriginalSubs = -> [Pocket037]
  Originals = -> [Pocket037]
  ParallelTransform = true
  Placement = pos=(0,0,0) rot=(1,0,0;1.5708rad)
  Refine = true
  SubTransform = true
  Suppress = false
  TreeRank = 0
  ValidateShape = true
  _Version = 0
FEATURE [Sketcher::SketchObject] Sketch100
  ArcFitTolerance = 0
  ExternalBSplineMaxDegree = 0
  ExternalBSplineTolerance = 0
  FixShape = 1
  FullyConstrained = true
  InternalTolerance = 1e-06
  InvalidShape = false
  MakeInternals = false
  MapMode = 5
  Placement = pos=(0,0,0) rot=(1,0,0;1.5708rad)
  TreeRank = 0
  ValidateShape = false
  sketch-geometry (1):
    g0: Circle CenterX=0 CenterY=-24 CenterZ=0 NormalX=0 NormalY=0 NormalZ=1 AngleXU=0 Radius=1.6
  constraints (3):
    c: PointOnObject(g0,g-2)
    c: Diameter(g0) = 3.2
    c: DistanceY(g0) = -24
FEATURE [PartDesign::Pocket] Pocket038
  AddSubType = 1
  AutoTaperInnerAngle = true
  BaseFeature = -> PolarPattern019
  CheckUpToFaceLimits = true
  ClaimChildren = false
  Direction = (0,1,0)
  Fit = 0
  FitJoin = 0
  FixShape = 1
  InnerFit = 0
  InnerFitJoin = 0
  InvalidShape = false
  Length = 5
  Length2 = 100
  Midplane = true
  NewSolid = false
  Placement = pos=(0,0,0) rot=(1,0,0;1.5708rad)
  Profile = -> Sketch100
  Refine = true
  Suppress = false
  TaperInnerAngle = 0
  TaperInnerAngleRev = 0
  TreeRank = 0
  Type = 1
  ValidateShape = true
  _ProfileBasedVersion = 0
  _Version = 0
FEATURE [PartDesign::PolarPattern] PolarPattern020
  AddSubType = 0
  Angle = 360
  Axis = -> Sketch100 [N_Axis]
  BaseFeature = -> Pocket038
  CopyShape = true
  FixShape = 1
  InvalidShape = false
  NewSolid = false
  Occurrences = 5
  OriginalSubs = -> [Pocket038]
  Originals = -> [Pocket038]
  ParallelTransform = true
  Placement = pos=(0,0,0) rot=(1,0,0;1.5708rad)
  Refine = true
  SubTransform = true
  Suppress = false
  TreeRank = 0
  ValidateShape = true
  _Version = 0
FEATURE [PartDesign::Body] Body047  label="MainPlate"
  AutoGroupSolids = false
  ClaimAllChildren = false
  ExportMode = 0
  FixShape = 1
  Group = -> [Sketch095,Pad057,Sketch096,Pad058,Sketch097,Pocket036,Sketch098,PolarPattern017,Pad059,PolarPattern018,Sketch099,Pocket037,PolarPattern019,Sketch100,Pocket038,PolarPattern020]
  InvalidShape = false
  Origin = -> Origin071
  SingleSolid = true
  Tip = -> PolarPattern020
  TreeRank = 0
  ValidateShape = false
  _ExportChildren = -> [Pad057,Pad058,Pocket036,PolarPattern017,Pad059,PolarPattern018,Pocket037,PolarPattern019,Pocket038,PolarPattern020]
  _GroupVersion = 1
COMPONENT P20 — recipe-attached ("17HS24-2104S", modeled in this document).
Construction recipe (the document's own serialized feature program — sketch geometry with constraints, then the solid features built on it; lengths are millimeters unless a unit is written):

FEATURE [Sketcher::SketchObject] Sketch
  ArcFitTolerance = 0
  ExternalBSplineMaxDegree = 0
  ExternalBSplineTolerance = 0
  FixShape = 1
  FullyConstrained = true
  InternalTolerance = 1e-06
  InvalidShape = false
  MakeInternals = false
  MapMode = 5
  Placement = pos=(0,0,0) rot=(1,0,0;1.5708rad)
  TreeRank = 0
  ValidateShape = false
  sketch-geometry (5):
    g0: LineSegment StartX=-21.15 StartY=-21.15 StartZ=0 EndX=21.15 EndY=-21.15 EndZ=0
    g1: LineSegment StartX=21.15 StartY=-21.15 StartZ=0 EndX=21.15 EndY=21.15 EndZ=0
    g2: LineSegment StartX=21.15 StartY=21.15 StartZ=0 EndX=-21.15 EndY=21.15 EndZ=0
    g3: LineSegment StartX=-21.15 StartY=21.15 StartZ=0 EndX=-21.15 EndY=-21.15 EndZ=0
    g4: GeomPoint [constr] X=0 Y=1e-16 Z=0
  constraints (12):
    c: Coincident(g0,g1)
    c: Coincident(g1,g2)
    c: Coincident(g2,g3)
    c: Coincident(g3,g0)
    c: Horizontal(g0)
    c: Horizontal(g2)
    c: Vertical(g1)
    c: Vertical(g3)
    c: Symmetric(g2,g0,g4)
    c: Coincident(g4,g-1)
    c: Equal(g2,g1)
    c: DistanceX(g2,g2) = 42.3
FEATURE [PartDesign::Pad] Pad
  AddSubType = 0
  AutoTaperInnerAngle = true
  CheckUpToFaceLimits = true
  ClaimChildren = false
  Direction = (0,-1,0)
  Fit = 0
  FitJoin = 0
  FixShape = 1
  InnerFit = 0
  InnerFitJoin = 0
  InvalidShape = false
  Length = 60
  Length2 = 10
  NewSolid = false
  Placement = pos=(0,0,0) rot=(1,0,0;1.5708rad)
  Profile = -> Sketch
  ReferenceAxis = -> Sketch [N_Axis]
  Refine = true
  Reversed = true
  Suppress = false
  TaperInnerAngle = 0
  TaperInnerAngleRev = 0
  TreeRank = 0
  Type = 0
  ValidateShape = true
  _ProfileBasedVersion = 0
FEATURE [Sketcher::SketchObject] Sketch001
  ArcFitTolerance = 0
  AttachmentSupport = -> [Pad]
  ExternalBSplineMaxDegree = 0
  ExternalBSplineTolerance = 0
  FixShape = 1
  FullyConstrained = true
  InternalTolerance = 1e-06
  InvalidShape = false
  MakeInternals = false
  MapMode = 5
  Placement = pos=(0,0,0) rot=(1,0,0;1.5708rad)
  Support = -> [Pad]
  TreeRank = 0
  ValidateShape = false
  sketch-geometry (1):
    g0: Circle CenterX=0 CenterY=0 CenterZ=0 NormalX=0 NormalY=0 NormalZ=1 AngleXU=0 Radius=11
  constraints (2):
    c: Coincident(g0,g-1)
    c: Diameter(g0) = 22
FEATURE [PartDesign::Pad] Pad001
  AddSubType = 0
  AutoTaperInnerAngle = true
  BaseFeature = -> Pad
  CheckUpToFaceLimits = true
  ClaimChildren = false
  Direction = (0,-1,-2e-16)
  Fit = 0
  FitJoin = 0
  FixShape = 1
  InnerFit = 0
  InnerFitJoin = 0
  InvalidShape = false
  Length = 2
  Length2 = 10
  NewSolid = false
  Placement = pos=(0,0,0) rot=(1,0,0;1.5708rad)
  Profile = -> Sketch001
  ReferenceAxis = -> Sketch001 [N_Axis]
  Refine = true
  Suppress = false
  TaperInnerAngle = 0
  TaperInnerAngleRev = 0
  TreeRank = 0
  Type = 0
  ValidateShape = true
  _ProfileBasedVersion = 0
FEATURE [Sketcher::SketchObject] Sketch002
  ArcFitTolerance = 0
  AttachmentSupport = -> [Pad001]
  ExternalBSplineMaxDegree = 0
  ExternalBSplineTolerance = 0
  FixShape = 1
  FullyConstrained = true
  InternalTolerance = 1e-06
  InvalidShape = false
  MakeInternals = false
  MapMode = 5
  Placement = pos=(0,0,0) rot=(1,0,0;1.5708rad)
  Support = -> [Pad001]
  TreeRank = 0
  ValidateShape = false
  sketch-geometry (1):
    g0: Circle CenterX=0 CenterY=0 CenterZ=0 NormalX=0 NormalY=0 NormalZ=1 AngleXU=0 Radius=2.5
  constraints (2):
    c: Coincident(g0,g-1)
    c: Diameter(g0) = 5
FEATURE [PartDesign::Pad] Pad002
  AddSubType = 0
  AutoTaperInnerAngle = true
  BaseFeature = -> Pad001
  CheckUpToFaceLimits = true
  ClaimChildren = false
  Direction = (0,-1,-7e-16)
  Fit = 0
  FitJoin = 0
  FixShape = 1
  InnerFit = 0
  InnerFitJoin = 0
  InvalidShape = false
  Length = 24
  Length2 = 10
  NewSolid = false
  Placement = pos=(0,0,0) rot=(1,0,0;1.5708rad)
  Profile = -> Sketch002
  ReferenceAxis = -> Sketch002 [N_Axis]
  Refine = true
  Suppress = false
  TaperInnerAngle = 0
  TaperInnerAngleRev = 0
  TreeRank = 0
  Type = 0
  ValidateShape = true
  _ProfileBasedVersion = 0
FEATURE [Sketcher::SketchObject] Sketch003
  ArcFitTolerance = 0
  ExternalBSplineMaxDegree = 0
  ExternalBSplineTolerance = 0
  ExternalGeometry = -> [Pad002]
  FixShape = 1
  FullyConstrained = true
  InternalTolerance = 1e-06
  InvalidShape = false
  MakeInternals = false
  MapMode = 5
  Placement = pos=(0,0,0) rot=(0.57735,0.57735,0.57735;2.0944rad)
  TreeRank = 0
  ValidateShape = false
  sketch-geometry (4):
    g0: LineSegment StartX=-24 StartY=2.5 StartZ=0 EndX=-24 EndY=2 EndZ=0
    g1: LineSegment StartX=-24 StartY=2 StartZ=0 EndX=-9 EndY=2 EndZ=0
    g2: LineSegment StartX=-9 StartY=2 StartZ=0 EndX=-9 EndY=2.5 EndZ=0
    g3: LineSegment StartX=-9 StartY=2.5 StartZ=0 EndX=-24 EndY=2.5 EndZ=0
  constraints (11):
    c: Coincident(g0,g1)
    c: Coincident(g1,g2)
    c: Coincident(g2,g3)
    c: Coincident(g3,g0)
    c: Vertical(g0)
    c: Vertical(g2)
    c: Horizontal(g1)
    c: Horizontal(g3)
    c: Coincident(g0,g-3)
    c: Distance(g0,g-3) = 4.5
    c: DistanceX(g1,g1) = 15
FEATURE [PartDesign::Pocket] Pocket
  AddSubType = 1
  AutoTaperInnerAngle = true
  BaseFeature = -> Pad002
  CheckUpToFaceLimits = true
  ClaimChildren = false
  Direction = (-1,-1e-16,1e-16)
  Fit = 0
  FitJoin = 0
  FixShape = 1
  InnerFit = 0
  InnerFitJoin = 0
  InvalidShape = false
  Length = 5
  Length2 = 5
  Midplane = true
  NewSolid = false
  Placement = pos=(0,0,0) rot=(1,0,0;1.5708rad)
  Profile = -> Sketch003
  ReferenceAxis = -> Sketch003 [N_Axis]
  Refine = true
  Suppress = false
  TaperInnerAngle = 0
  TaperInnerAngleRev = 0
  TreeRank = 0
  Type = 1
  ValidateShape = true
  _ProfileBasedVersion = 0
  _Version = 0
FEATURE [Sketcher::SketchObject] Sketch004
  ArcFitTolerance = 0
  ExternalBSplineMaxDegree = 0
  ExternalBSplineTolerance = 0
  FixShape = 1
  FullyConstrained = true
  InternalTolerance = 1e-06
  InvalidShape = false
  MakeInternals = false
  MapMode = 5
  Placement = pos=(0,0,0) rot=(1,0,0;1.5708rad)
  TreeRank = 0
  ValidateShape = false
  sketch-geometry (9):
    g0: LineSegment [constr] StartX=-15.5 StartY=-15.5 StartZ=0 EndX=15.5 EndY=-15.5 EndZ=0
    g1: LineSegment [constr] StartX=15.5 StartY=-15.5 StartZ=0 EndX=15.5 EndY=15.5 EndZ=0
    g2: LineSegment [constr] StartX=15.5 StartY=15.5 StartZ=0 EndX=-15.5 EndY=15.5 EndZ=0
    g3: LineSegment [constr] StartX=-15.5 StartY=15.5 StartZ=0 EndX=-15.5 EndY=-15.5 EndZ=0
    g4: GeomPoint [constr] X=0 Y=0 Z=0
    g5: Circle CenterX=-15.5 CenterY=15.5 CenterZ=0 NormalX=0 NormalY=0 NormalZ=1 AngleXU=0 Radius=1.5
    g6: Circle CenterX=15.5 CenterY=15.5 CenterZ=0 NormalX=0 NormalY=0 NormalZ=1 AngleXU=0 Radius=1.5
    g7: Circle CenterX=15.5 CenterY=-15.5 CenterZ=0 NormalX=0 NormalY=0 NormalZ=1 AngleXU=0 Radius=1.5
    g8: Circle CenterX=-15.5 CenterY=-15.5 CenterZ=0 NormalX=0 NormalY=0 NormalZ=1 AngleXU=0 Radius=1.5
  constraints (20):
    c: Coincident(g0,g1)
    c: Coincident(g1,g2)
    c: Coincident(g2,g3)
    c: Coincident(g3,g0)
    c: Horizontal(g0)
    c: Horizontal(g2)
    c: Vertical(g1)
    c: Vertical(g3)
    c: Symmetric(g2,g0,g4)
    c: Coincident(g4,g-1)
    c: Equal(g1,g2)
    c: DistanceX(g2,g2) = 31
    c: Coincident(g5,g2)
    c: Coincident(g6,g1)
    c: Coincident(g7,g0)
    c: Coincident(g8,g0)
    c: Equal(g8,g5)
    c: Equal(g5,g6)
    c: Equal(g6,g7)
    c: Diameter(g6) = 3
FEATURE [PartDesign::Pocket] Pocket001
  AddSubType = 1
  AutoTaperInnerAngle = true
  BaseFeature = -> Pocket
  CheckUpToFaceLimits = true
  ClaimChildren = false
  Direction = (0,1,0)
  Fit = 0
  FitJoin = 0
  FixShape = 1
  InnerFit = 0
  InnerFitJoin = 0
  InvalidShape = false
  Length = 20
  Length2 = 5
  NewSolid = false
  Placement = pos=(0,0,0) rot=(1,0,0;1.5708rad)
  Profile = -> Sketch004
  ReferenceAxis = -> Sketch004 [N_Axis]
  Refine = true
  Suppress = false
  TaperInnerAngle = 0
  TaperInnerAngleRev = 0
  TreeRank = 0
  Type = 0
  ValidateShape = true
  _ProfileBasedVersion = 0
  _Version = 0
FEATURE [PartDesign::Chamfer] Chamfer
  AddSubType = 0
  Angle = 45
  Base = -> Pocket001 [Edge35]
  BaseFeature = -> Pocket001
  ChamferType = 0
  FixShape = 1
  FlipDirection = false
  InvalidShape = false
  NewSolid = false
  Placement = pos=(0,0,0) rot=(1,0,0;1.5708rad)
  Refine = true
  Size = 0.2
  Size2 = 1
  SupportTransform = false
  Suppress = false
  TreeRank = 0
  UseAllEdges = false
  ValidateShape = true
FEATURE [PartDesign::Chamfer] Chamfer001
  AddSubType = 0
  Angle = 45
  Base = -> Chamfer [Edge32,Edge28,Edge30,Edge27]
  BaseFeature = -> Chamfer
  ChamferType = 0
  FixShape = 1
  FlipDirection = false
  InvalidShape = false
  NewSolid = false
  Placement = pos=(0,0,0) rot=(1,0,0;1.5708rad)
  Refine = true
  Size = 5
  Size2 = 1
  SupportTransform = false
  Suppress = false
  TreeRank = 0
  UseAllEdges = false
  ValidateShape = true
FEATURE [PartDesign::Body] Body  label="Simple-17HS24-2104S"
  AutoGroupSolids = false
  ClaimAllChildren = false
  ExportMode = 0
  FixShape = 1
  Group = -> [Sketch,Pad,Sketch001,Pad001,Sketch002,Pad002,Sketch003,Pocket,Sketch004,Pocket001,Chamfer,Chamfer001]
  InvalidShape = false
  Origin = -> Origin
  SingleSolid = true
  Tip = -> Chamfer001
  TreeRank = 0
  ValidateShape = false
  _ExportChildren = -> [Pad,Pad001,Pad002,Pocket,Pocket001,Chamfer,Chamfer001]
  _GroupVersion = 1
COMPONENT P21 — recipe-attached ("MF128", modeled in this document).
Construction recipe (the document's own serialized feature program — sketch geometry with constraints, then the solid features built on it; lengths are millimeters unless a unit is written):

FEATURE [Sketcher::SketchObject] Sketch116
  ArcFitTolerance = 0
  ExternalBSplineMaxDegree = 0
  ExternalBSplineTolerance = 0
  FixShape = 1
  FullyConstrained = true
  InternalTolerance = 1e-06
  InvalidShape = false
  MakeInternals = false
  MapMode = 5
  TreeRank = 0
  ValidateShape = false
  sketch-geometry (10):
    g0: LineSegment StartX=-6.8 StartY=0 StartZ=0 EndX=-6.8 EndY=0.8 EndZ=0
    g1: LineSegment StartX=-6.8 StartY=0.8 StartZ=0 EndX=-5.4 EndY=0.8 EndZ=0
    g2: LineSegment StartX=-5.4 StartY=0.8 StartZ=0 EndX=-5.4 EndY=-2.7 EndZ=0
    g3: LineSegment StartX=-5.4 StartY=-2.7 StartZ=0 EndX=-6 EndY=-2.7 EndZ=0
    g4: LineSegment StartX=-6 StartY=-2.7 StartZ=0 EndX=-6 EndY=0 EndZ=0
    g5: LineSegment StartX=-6 StartY=0 StartZ=0 EndX=-6.8 EndY=0 EndZ=0
    g6: LineSegment StartX=-4.6 StartY=0.8 StartZ=0 EndX=-4 EndY=0.8 EndZ=0
    g7: LineSegment StartX=-4 StartY=0.8 StartZ=0 EndX=-4 EndY=-2.7 EndZ=0
    g8: LineSegment StartX=-4 StartY=-2.7 StartZ=0 EndX=-4.6 EndY=-2.7 EndZ=0
    g9: LineSegment StartX=-4.6 StartY=-2.7 StartZ=0 EndX=-4.6 EndY=0.8 EndZ=0
  constraints (30):
    c: Vertical(g0)
    c: Coincident(g0,g1)
    c: Horizontal(g1)
    c: Coincident(g1,g2)
    c: Vertical(g2)
    c: Coincident(g2,g3)
    c: Horizontal(g3)
    c: Coincident(g3,g4)
    c: Vertical(g4)
    c: Coincident(g4,g5)
    c: Coincident(g5,g0)
    c: Horizontal(g5)
    c: Coincident(g6,g7)
    c: Coincident(g7,g8)
    c: Coincident(g8,g9)
    c: Coincident(g9,g6)
    c: Horizontal(g6)
    c: Horizontal(g8)
    c: Vertical(g7)
    c: Vertical(g9)
    c: PointOnObject(g6,g1)
    c: PointOnObject(g4,g-1)
    c: DistanceY(g2,g2) = 3.5
    c: PointOnObject(g8,g3)
    c: DistanceX(g3) = -6
    c: DistanceX(g6) = -4
    c: Equal(g3,g6)
    c: DistanceX(g6,g6) = 0.6
    c: DistanceX(g0) = -6.8
    c: DistanceY(g0,g0) = 0.8
FEATURE [PartDesign::Revolution] Revolution005
  AddSubType = 0
  Angle = 360
  Axis = (0,1,0)
  Base = (0,0,0)
  ClaimChildren = false
  Fit = 0
  FitJoin = 0
  FixShape = 1
  InnerFit = 0
  InnerFitJoin = 0
  InvalidShape = false
  NewSolid = false
  Profile = -> Sketch116
  ReferenceAxis = -> Sketch116 [V_Axis]
  Refine = true
  Suppress = false
  TreeRank = 0
  ValidateShape = true
  _ProfileBasedVersion = 0
FEATURE [PartDesign::Body] Body052  label="CoreMF128"
  AutoGroupSolids = false
  ClaimAllChildren = false
  ExportMode = 0
  FixShape = 1
  Group = -> [Sketch116,Revolution005]
  InvalidShape = false
  Origin = -> Origin016
  Tip = -> Revolution005
  TreeRank = 0
  ValidateShape = false
  _ExportChildren = -> [Revolution005]
  _GroupVersion = 1
FEATURE [Sketcher::SketchObject] Sketch117
  ArcFitTolerance = 0
  ExternalBSplineMaxDegree = 0
  ExternalBSplineTolerance = 0
  FixShape = 1
  FullyConstrained = true
  InternalTolerance = 1e-06
  InvalidShape = false
  MakeInternals = false
  MapMode = 5
  TreeRank = 0
  ValidateShape = false
  sketch-geometry (4):
    g0: LineSegment StartX=-5.5 StartY=0.55 StartZ=0 EndX=-4.5 EndY=0.55 EndZ=0
    g1: LineSegment StartX=-4.5 StartY=0.55 StartZ=0 EndX=-4.5 EndY=-2.45 EndZ=0
    g2: LineSegment StartX=-4.5 StartY=-2.45 StartZ=0 EndX=-5.5 EndY=-2.45 EndZ=0
    g3: LineSegment StartX=-5.5 StartY=-2.45 StartZ=0 EndX=-5.5 EndY=0.55 EndZ=0
  constraints (12):
    c: Coincident(g0,g1)
    c: Coincident(g1,g2)
    c: Coincident(g2,g3)
    c: Coincident(g3,g0)
    c: Horizontal(g0)
    c: Horizontal(g2)
    c: Vertical(g1)
    c: Vertical(g3)
    c: DistanceY(g3,g3) = 3
    c: DistanceX(g0,g0) = 1
    c: DistanceX(g0,g-1) = 4.5
    c: DistanceY(g-1,g0) = 0.55
FEATURE [PartDesign::Revolution] Revolution006
  AddSubType = 0
  Angle = 360
  Axis = (0,1,0)
  Base = (0,0,0)
  ClaimChildren = false
  Fit = 0
  FitJoin = 0
  FixShape = 1
  InnerFit = 0
  InnerFitJoin = 0
  InvalidShape = false
  NewSolid = false
  Profile = -> Sketch117
  ReferenceAxis = -> Sketch117 [V_Axis]
  Refine = true
  Suppress = false
  TreeRank = 0
  ValidateShape = true
  _ProfileBasedVersion = 0
FEATURE [PartDesign::Body] Body053  label="SleeveMF128"
  AutoGroupSolids = false
  ClaimAllChildren = false
  ExportMode = 0
  FixShape = 1
  Group = -> [Sketch117,Revolution006]
  InvalidShape = false
  Origin = -> Origin081
  SingleSolid = true
  Tip = -> Revolution006
  TreeRank = 0
  ValidateShape = false
  _ExportChildren = -> [Revolution006]
  _GroupVersion = 1
COMPONENT P22 — recipe-attached ("MF83", modeled in this document).
Construction recipe (the document's own serialized feature program — sketch geometry with constraints, then the solid features built on it; lengths are millimeters unless a unit is written):

FEATURE [Sketcher::SketchObject] Sketch160
  ArcFitTolerance = 0
  ExternalBSplineMaxDegree = 0
  ExternalBSplineTolerance = 0
  FixShape = 1
  FullyConstrained = true
  InternalTolerance = 1e-06
  InvalidShape = false
  MakeInternals = false
  MapMode = 5
  TreeRank = 0
  ValidateShape = false
  sketch-geometry (10):
    g0: LineSegment StartX=-4.6 StartY=0 StartZ=0 EndX=-4.6 EndY=0.6 EndZ=0
    g1: LineSegment StartX=-4.6 StartY=0.6 StartZ=0 EndX=-3.4 EndY=0.6 EndZ=0
    g2: LineSegment StartX=-3.4 StartY=0.6 StartZ=0 EndX=-3.4 EndY=-2.4 EndZ=0
    g3: LineSegment StartX=-3.4 StartY=-2.4 StartZ=0 EndX=-4 EndY=-2.4 EndZ=0
    g4: LineSegment StartX=-4 StartY=-2.4 StartZ=0 EndX=-4 EndY=0 EndZ=0
    g5: LineSegment StartX=-4 StartY=0 StartZ=0 EndX=-4.6 EndY=0 EndZ=0
    g6: LineSegment StartX=-2.1 StartY=0.6 StartZ=0 EndX=-1.5 EndY=0.6 EndZ=0
    g7: LineSegment StartX=-1.5 StartY=0.6 StartZ=0 EndX=-1.5 EndY=-2.4 EndZ=0
    g8: LineSegment StartX=-1.5 StartY=-2.4 StartZ=0 EndX=-2.1 EndY=-2.4 EndZ=0
    g9: LineSegment StartX=-2.1 StartY=-2.4 StartZ=0 EndX=-2.1 EndY=0.6 EndZ=0
  constraints (30):
    c: Vertical(g0)
    c: Coincident(g0,g1)
    c: Horizontal(g1)
    c: Coincident(g1,g2)
    c: Vertical(g2)
    c: Coincident(g2,g3)
    c: Horizontal(g3)
    c: Coincident(g3,g4)
    c: Vertical(g4)
    c: Coincident(g4,g5)
    c: Coincident(g5,g0)
    c: Horizontal(g5)
    c: Coincident(g6,g7)
    c: Coincident(g7,g8)
    c: Coincident(g8,g9)
    c: Coincident(g9,g6)
    c: Horizontal(g6)
    c: Horizontal(g8)
    c: Vertical(g7)
    c: Vertical(g9)
    c: PointOnObject(g6,g1)
    c: PointOnObject(g4,g-1)
    c: DistanceY(g2,g2) = 3
    c: PointOnObject(g8,g3)
    c: DistanceX(g3) = -4
    c: DistanceX(g6) = -1.5
    c: Equal(g3,g6)
    c: DistanceX(g6,g6) = 0.6
    c: DistanceX(g0) = -4.6
    c: DistanceY(g0,g0) = 0.6
FEATURE [PartDesign::Revolution] Revolution010
  AddSubType = 0
  Angle = 360
  Axis = (0,1,0)
  Base = (0,0,0)
  ClaimChildren = false
  Fit = 0
  FitJoin = 0
  FixShape = 1
  InnerFit = 0
  InnerFitJoin = 0
  InvalidShape = false
  NewSolid = false
  Profile = -> Sketch160
  ReferenceAxis = -> Sketch160 [V_Axis]
  Refine = true
  Suppress = false
  TreeRank = 0
  ValidateShape = true
  _ProfileBasedVersion = 0
FEATURE [PartDesign::Body] Body074  label="CoreMF83"
  AutoGroupSolids = false
  ClaimAllChildren = false
  ExportMode = 0
  FixShape = 1
  Group = -> [Sketch160,Revolution010]
  InvalidShape = false
  Origin = -> Origin158
  Placement = pos=(0,2.8e-14,0) rot=(0,0,1;0rad)
  Tip = -> Revolution010
  TreeRank = 0
  ValidateShape = false
  _ExportChildren = -> [Revolution010]
  _GroupVersion = 1
FEATURE [Sketcher::SketchObject] Sketch161
  ArcFitTolerance = 0
  ExternalBSplineMaxDegree = 0
  ExternalBSplineTolerance = 0
  FixShape = 1
  FullyConstrained = true
  InternalTolerance = 1e-06
  InvalidShape = false
  MakeInternals = false
  MapMode = 5
  TreeRank = 0
  ValidateShape = false
  sketch-geometry (4):
    g0: LineSegment StartX=-3.4 StartY=0.5 StartZ=0 EndX=-2.1 EndY=0.5 EndZ=0
    g1: LineSegment StartX=-2.1 StartY=0.5 StartZ=0 EndX=-2.1 EndY=-2.3 EndZ=0
    g2: LineSegment StartX=-2.1 StartY=-2.3 StartZ=0 EndX=-3.4 EndY=-2.3 EndZ=0
    g3: LineSegment StartX=-3.4 StartY=-2.3 StartZ=0 EndX=-3.4 EndY=0.5 EndZ=0
  constraints (12):
    c: Coincident(g0,g1)
    c: Coincident(g1,g2)
    c: Coincident(g2,g3)
    c: Coincident(g3,g0)
    c: Horizontal(g0)
    c: Horizontal(g2)
    c: Vertical(g1)
    c: Vertical(g3)
    c: DistanceY(g3,g3) = 2.8
    c: DistanceX(g0,g0) = 1.3
    c: DistanceX(g0,g-1) = 2.1
    c: DistanceY(g-1,g0) = 0.5
FEATURE [PartDesign::Revolution] Revolution011
  AddSubType = 0
  Angle = 360
  Axis = (1e-16,1,-1e-16)
  Base = (0,0,0)
  ClaimChildren = false
  Fit = 0
  FitJoin = 0
  FixShape = 1
  InnerFit = 0
  InnerFitJoin = 0
  InvalidShape = false
  NewSolid = false
  Profile = -> Sketch161
  ReferenceAxis = -> Y_Axis092
  Refine = true
  Suppress = false
  TreeRank = 0
  ValidateShape = true
  _ProfileBasedVersion = 0
FEATURE [PartDesign::Body] Body075  label="SleeveMF83"
  AutoGroupSolids = false
  ClaimAllChildren = false
  ExportMode = 0
  FixShape = 1
  Group = -> [Sketch161,Revolution011]
  InvalidShape = false
  Origin = -> Origin159
  Placement = pos=(0,2.8e-14,0) rot=(0,0,1;0rad)
  SingleSolid = true
  Tip = -> Revolution011
  TreeRank = 0
  ValidateShape = false
  _ExportChildren = -> [Revolution011]
  _GroupVersion = 1
COMPONENT P23 — recipe-attached ("633ZZ", modeled in this document).
Construction recipe (the document's own serialized feature program — sketch geometry with constraints, then the solid features built on it; lengths are millimeters unless a unit is written):

FEATURE [Sketcher::SketchObject] Sketch169
  ArcFitTolerance = 0
  ExternalBSplineMaxDegree = 0
  ExternalBSplineTolerance = 0
  FixShape = 1
  FullyConstrained = true
  InternalTolerance = 1e-06
  InvalidShape = false
  MakeInternals = false
  MapMode = 5
  Placement = pos=(0,0,0) rot=(1,0,0;1.5708rad)
  TreeRank = 0
  ValidateShape = false
  sketch-geometry (12):
    g0: LineSegment StartX=-5.5 StartY=1.2718e-12 StartZ=0 EndX=-6.5 EndY=1.052e-12 EndZ=0
    g1: LineSegment StartX=-6.5 StartY=1.052e-12 StartZ=0 EndX=-6.5 EndY=5 EndZ=0
    g2: LineSegment StartX=-6.5 StartY=5 StartZ=0 EndX=-5.5 EndY=5 EndZ=0
    g3: LineSegment StartX=-5.5 StartY=5 StartZ=0 EndX=-5.5 EndY=4.6 EndZ=0
    g4: LineSegment StartX=-5.5 StartY=4.6 StartZ=0 EndX=-2.5 EndY=4.6 EndZ=0
    g5: LineSegment StartX=-2.5 StartY=4.6 StartZ=0 EndX=-2.5 EndY=5 EndZ=0
    g6: LineSegment StartX=-2.5 StartY=5 StartZ=0 EndX=-1.5 EndY=5 EndZ=0
    g7: LineSegment StartX=-1.5 StartY=5 StartZ=0 EndX=-1.5 EndY=0 EndZ=0
    g8: LineSegment StartX=-1.5 StartY=0 StartZ=0 EndX=-2.5 EndY=0 EndZ=0
    g9: LineSegment StartX=-2.5 StartY=0 StartZ=0 EndX=-2.5 EndY=0.4 EndZ=0
    g10: LineSegment StartX=-2.5 StartY=0.4 StartZ=0 EndX=-5.5 EndY=0.4 EndZ=0
    g11: LineSegment StartX=-5.5 StartY=0.4 StartZ=0 EndX=-5.5 EndY=1.2718e-12 EndZ=0
  constraints (36):
    c: PointOnObject(g0,g-1)
    c: PointOnObject(g0,g-1)
    c: Coincident(g0,g1)
    c: Vertical(g1)
    c: Coincident(g1,g2)
    c: Horizontal(g2)
    c: Coincident(g2,g3)
    c: Vertical(g3)
    c: Coincident(g3,g4)
    c: Horizontal(g4)
    c: Coincident(g4,g5)
    c: Vertical(g5)
    c: Coincident(g5,g6)
    c: Horizontal(g6)
    c: Coincident(g6,g7)
    c: PointOnObject(g7,g-1)
    c: Vertical(g7)
    c: Coincident(g7,g8)
    c: PointOnObject(g8,g-1)
    c: Coincident(g8,g9)
    c: Vertical(g9)
    c: Coincident(g9,g10)
    c: Horizontal(g10)
    c: Coincident(g10,g11)
    c: Coincident(g11,g0)
    c: Vertical(g11)
    c: DistanceX(g7) = -1.5
    c: DistanceX(g0) = -6.5
    c: Equal(g8,g0)
    c: Equal(g2,g6)
    c: Equal(g4,g10)
    c: Equal(g3,g11)
    c: DistanceY(g3,g3) = 0.4
    c: DistanceX(g8,g8) = 1
    c: DistanceY(g1,g1) = 5
    c: PointOnObject(g2,g6)
FEATURE [PartDesign::Revolution] Revolution012
  AddSubType = 0
  Angle = 360
  Axis = (0,0,1)
  Base = (0,0,0)
  ClaimChildren = false
  Fit = 0
  FitJoin = 0
  FixShape = 1
  InnerFit = 0
  InnerFitJoin = 0
  InvalidShape = false
  NewSolid = false
  Placement = pos=(0,0,0) rot=(1,0,0;1.5708rad)
  Profile = -> Sketch169
  ReferenceAxis = -> Sketch169 [V_Axis]
  Refine = true
  Suppress = false
  TreeRank = 0
  ValidateShape = true
  _ProfileBasedVersion = 0
FEATURE [PartDesign::Body] Body080  label="CoreMR149"
  AutoGroupSolids = false
  ClaimAllChildren = false
  ExportMode = 0
  FixShape = 1
  Group = -> [Sketch169,Revolution012]
  InvalidShape = false
  Origin = -> Origin166
  SingleSolid = true
  Tip = -> Revolution012
  TreeRank = 0
  ValidateShape = false
  _ExportChildren = -> [Revolution012]
  _GroupVersion = 1
FEATURE [Sketcher::SketchObject] Sketch170
  ArcFitTolerance = 0
  ExternalBSplineMaxDegree = 0
  ExternalBSplineTolerance = 0
  FixShape = 1
  FullyConstrained = true
  InternalTolerance = 1e-06
  InvalidShape = false
  MakeInternals = false
  MapMode = 5
  Placement = pos=(0,0,0) rot=(1,0,0;1.5708rad)
  TreeRank = 0
  ValidateShape = false
  sketch-geometry (4):
    g0: LineSegment StartX=-5.5 StartY=5 StartZ=0 EndX=-2.5 EndY=5 EndZ=0
    g1: LineSegment StartX=-2.5 StartY=5 StartZ=0 EndX=-2.5 EndY=0 EndZ=0
    g2: LineSegment StartX=-2.5 StartY=3e-16 StartZ=0 EndX=-5.5 EndY=3e-16 EndZ=0
    g3: LineSegment StartX=-5.5 StartY=3e-16 StartZ=0 EndX=-5.5 EndY=5 EndZ=0
  constraints (12):
    c: Coincident(g0,g1)
    c: Coincident(g1,g2)
    c: Coincident(g2,g3)
    c: Coincident(g3,g0)
    c: Horizontal(g0)
    c: Horizontal(g2)
    c: Vertical(g1)
    c: Vertical(g3)
    c: PointOnObject(g1,g-1)
    c: DistanceY(g3,g3) = 5
    c: DistanceX(g1) = -2.5
    c: DistanceX(g2) = -5.5
FEATURE [PartDesign::Revolution] Revolution013
  AddSubType = 0
  Angle = 360
  Axis = (0,0,1)
  Base = (0,0,0)
  ClaimChildren = false
  Fit = 0
  FitJoin = 0
  FixShape = 1
  InnerFit = 0
  InnerFitJoin = 0
  InvalidShape = false
  NewSolid = false
  Placement = pos=(0,0,0) rot=(1,0,0;1.5708rad)
  Profile = -> Sketch170
  ReferenceAxis = -> Sketch170 [V_Axis]
  Refine = true
  Suppress = false
  TreeRank = 0
  ValidateShape = true
  _ProfileBasedVersion = 0
FEATURE [PartDesign::Body] Body081  label="Sleeve001"
  AutoGroupSolids = false
  ClaimAllChildren = false
  ExportMode = 0
  FixShape = 1
  Group = -> [Sketch170,Revolution013]
  InvalidShape = false
  Origin = -> Origin167
  SingleSolid = true
  Tip = -> Revolution013
  TreeRank = 0
  ValidateShape = false
  _ExportChildren = -> [Revolution013]
  _GroupVersion = 1
COMPONENT P24 — recipe-attached ("BAU-2195813", modeled in this document).
Construction recipe (the document's own serialized feature program — sketch geometry with constraints, then the solid features built on it; lengths are millimeters unless a unit is written):

FEATURE [Sketcher::SketchObject] Sketch171
  ArcFitTolerance = 0
  ExternalBSplineMaxDegree = 0
  ExternalBSplineTolerance = 0
  FixShape = 1
  FullyConstrained = true
  InternalTolerance = 1e-06
  InvalidShape = false
  MakeInternals = false
  MapMode = 5
  TreeRank = 0
  ValidateShape = false
  sketch-geometry (1):
    g0: Circle CenterX=0 CenterY=0 CenterZ=0 NormalX=0 NormalY=0 NormalZ=1 AngleXU=0 Radius=9
  constraints (2):
    c: Coincident(g0,g-1)
    c: Diameter(g0) = 18
FEATURE [PartDesign::Pad] Pad073
  AddSubType = 0
  AlongSketchNormal = false
  AutoTaperInnerAngle = true
  CheckUpToFaceLimits = true
  ClaimChildren = false
  Direction = (0,0,1)
  Fit = 0
  FitJoin = 0
  FixShape = 1
  InnerFit = 0
  InnerFitJoin = 0
  InvalidShape = false
  Length = 9
  Length2 = 100
  NewSolid = false
  Profile = -> Sketch171
  Refine = true
  Suppress = false
  TaperInnerAngle = 0
  TaperInnerAngleRev = 0
  TreeRank = 0
  Type = 0
  ValidateShape = true
  _ProfileBasedVersion = 0
FEATURE [PartDesign::Fillet] Fillet041
  AddSubType = 0
  Base = -> Pad073 [Edge3]
  BaseFeature = -> Pad073
  FixShape = 1
  InvalidShape = false
  NewSolid = false
  Radius = 0.4
  Refine = true
  SupportTransform = false
  Suppress = false
  TreeRank = 0
  UseAllEdges = false
  ValidateShape = true
FEATURE [Sketcher::SketchObject] Sketch172
  ArcFitTolerance = 0
  ExternalBSplineMaxDegree = 0
  ExternalBSplineTolerance = 0
  FixShape = 1
  FullyConstrained = true
  InternalTolerance = 1e-06
  InvalidShape = false
  MakeInternals = false
  MapMode = 5
  Placement = pos=(0,0,0) rot=(1,0,0;1.5708rad)
  TreeRank = 0
  ValidateShape = false
  sketch-geometry (8):
    g0: LineSegment StartX=0 StartY=-2.075e-13 StartZ=0 EndX=7.75 EndY=-2.075e-13 EndZ=0
    g1: LineSegment StartX=7.75 StartY=-2.075e-13 StartZ=0 EndX=7.75 EndY=-3 EndZ=0
    g2: LineSegment StartX=7.75 StartY=-3 StartZ=0 EndX=8.8 EndY=-3 EndZ=0
    g3: LineSegment StartX=8.8 StartY=-3 StartZ=0 EndX=8.8 EndY=-10.5 EndZ=0
    g4: LineSegment StartX=8.8 StartY=-10.5 StartZ=0 EndX=7.75 EndY=-10.5 EndZ=0
    g5: LineSegment StartX=7.75 StartY=-10.5 StartZ=0 EndX=7.75 EndY=-19 EndZ=0
    g6: LineSegment StartX=7.75 StartY=-19 StartZ=0 EndX=0 EndY=-19 EndZ=0
    g7: LineSegment StartX=0 StartY=-19 StartZ=0 EndX=0 EndY=-2.061e-13 EndZ=0
  constraints (23):
    c: Coincident(g-1,g0)
    c: Horizontal(g0)
    c: Coincident(g0,g1)
    c: Vertical(g1)
    c: Coincident(g1,g2)
    c: Horizontal(g2)
    c: Coincident(g2,g3)
    c: Vertical(g3)
    c: Coincident(g3,g4)
    c: Coincident(g4,g5)
    c: Vertical(g5)
    c: Coincident(g5,g6)
    c: PointOnObject(g6,g-2)
    c: Horizontal(g6)
    c: Coincident(g6,g7)
    c: Coincident(g7,g0)
    c: DistanceY(g1,g1) = 3
    c: DistanceX(g2) = 8.8
    c: DistanceX(g1) = 7.75
    c: PointOnObject(g5,g1)
    c: DistanceY(g3,g3) = 7.5
    c: Horizontal(g4)
    c: DistanceY(g7,g7) = 19
FEATURE [PartDesign::Revolution] Revolution014
  AddSubType = 0
  Angle = 360
  Axis = (0,0,1)
  Base = (0,0,0)
  BaseFeature = -> Fillet041
  ClaimChildren = false
  Fit = 0
  FitJoin = 0
  FixShape = 1
  InnerFit = 0
  InnerFitJoin = 0
  InvalidShape = false
  NewSolid = false
  Profile = -> Sketch172
  ReferenceAxis = -> Sketch172 [V_Axis]
  Refine = true
  Reversed = true
  Suppress = false
  TreeRank = 0
  ValidateShape = true
  _ProfileBasedVersion = 0
FEATURE [PartDesign::Body] Body082  label="MainBody"
  AutoGroupSolids = false
  ClaimAllChildren = false
  ExportMode = 0
  FixShape = 1
  Group = -> [Sketch171,Pad073,Fillet041,Sketch172,Revolution014]
  InvalidShape = false
  Origin = -> Origin169
  SingleSolid = true
  Tip = -> Revolution014
  TreeRank = 0
  ValidateShape = false
  _ExportChildren = -> [Pad073,Fillet041,Revolution014]
  _GroupVersion = 1
FEATURE [Sketcher::SketchObject] Sketch173
  ArcFitTolerance = 0
  ExternalBSplineMaxDegree = 0
  ExternalBSplineTolerance = 0
  FixShape = 1
  FullyConstrained = true
  InternalTolerance = 1e-06
  InvalidShape = false
  MakeInternals = false
  MapMode = 5
  Placement = pos=(0,-4e-15,-19) rot=(1,0,0;3.14159rad)
  TreeRank = 0
  ValidateShape = false
  sketch-geometry (5):
    g0: LineSegment StartX=9.5 StartY=9.5 StartZ=0 EndX=-9.5 EndY=9.5 EndZ=0
    g1: LineSegment StartX=-9.5 StartY=9.5 StartZ=0 EndX=-9.5 EndY=-9.5 EndZ=0
    g2: LineSegment StartX=-9.5 StartY=-9.5 StartZ=0 EndX=9.5 EndY=-9.5 EndZ=0
    g3: LineSegment StartX=9.5 StartY=-9.5 StartZ=0 EndX=9.5 EndY=9.5 EndZ=0
    g4: Circle [constr] CenterX=-1.2948e-12 CenterY=-4.7939e-12 CenterZ=0 NormalX=0 NormalY=0 NormalZ=1 AngleXU=0 Radius=13.435
  constraints (14):
    c: Coincident(g0,g1)
    c: Coincident(g1,g2)
    c: Coincident(g2,g3)
    c: Coincident(g3,g0)
    c: Equal(g0,g1)
    c: Equal(g0,g2)
    c: Equal(g0,g3)
    c: PointOnObject(g0,g4)
    c: PointOnObject(g1,g4)
    c: PointOnObject(g2,g4)
    c: PointOnObject(g3,g4)
    c: Coincident(g4,g-1)
    c: Horizontal(g0)
    c: DistanceX(g0,g0) = 19
FEATURE [PartDesign::Pad] Pad074
  AddSubType = 0
  AlongSketchNormal = false
  AutoTaperInnerAngle = true
  CheckUpToFaceLimits = true
  ClaimChildren = false
  Direction = (0,-1e-16,-1)
  Fit = 0
  FitJoin = 0
  FixShape = 1
  InnerFit = 0
  InnerFitJoin = 0
  InvalidShape = false
  Length = 14.5
  Length2 = 100
  NewSolid = false
  Placement = pos=(0,-4e-15,-19) rot=(1,0,0;3.14159rad)
  Profile = -> Sketch173
  Refine = true
  Suppress = false
  TaperInnerAngle = 0
  TaperInnerAngleRev = 0
  TreeRank = 0
  Type = 0
  ValidateShape = true
  _ProfileBasedVersion = 0
FEATURE [PartDesign::Fillet] Fillet042
  AddSubType = 0
  Base = -> Pad074 [Edge11,Edge6]
  BaseFeature = -> Pad074
  FixShape = 1
  InvalidShape = false
  NewSolid = false
  Placement = pos=(0,-4e-15,-19) rot=(1,0,0;3.14159rad)
  Radius = 1
  Refine = true
  SupportTransform = false
  Suppress = false
  TreeRank = 0
  UseAllEdges = false
  ValidateShape = true
FEATURE [PartDesign::Body] Body083  label="ElectronicBody"
  AutoGroupSolids = false
  ClaimAllChildren = false
  ExportMode = 0
  FixShape = 1
  Group = -> [Sketch173,Pad074,Fillet042]
  InvalidShape = false
  Origin = -> Origin170
  SingleSolid = true
  Tip = -> Fillet042
  TreeRank = 0
  ValidateShape = false
  _ExportChildren = -> [Pad074,Fillet042]
  _GroupVersion = 1
FEATURE [Sketcher::SketchObject] Sketch174
  ArcFitTolerance = 0
  AttachmentSupport = -> [Fillet042]
  ExternalBSplineMaxDegree = 0
  ExternalBSplineTolerance = 0
  FixShape = 1
  FullyConstrained = true
  InternalTolerance = 1e-06
  InvalidShape = false
  MakeInternals = false
  MapMode = 5
  Placement = pos=(0,-4e-15,-33.5) rot=(1,0,0;3.14159rad)
  Support = -> [Fillet042]
  TreeRank = 0
  ValidateShape = false
  sketch-geometry (16):
    g0: LineSegment StartX=-7.75 StartY=7.3 StartZ=0 EndX=-7.25 EndY=7.3 EndZ=0
    g1: LineSegment StartX=-7.25 StartY=7.3 StartZ=0 EndX=-7.25 EndY=4.5 EndZ=0
    g2: LineSegment StartX=-7.25 StartY=4.5 StartZ=0 EndX=-7.75 EndY=4.5 EndZ=0
    g3: LineSegment StartX=-7.75 StartY=4.5 StartZ=0 EndX=-7.75 EndY=7.3 EndZ=0
    g4: LineSegment StartX=7.25 StartY=7.3 StartZ=0 EndX=7.75 EndY=7.3 EndZ=0
    g5: LineSegment StartX=7.75 StartY=7.3 StartZ=0 EndX=7.75 EndY=4.5 EndZ=0
    g6: LineSegment StartX=7.75 StartY=4.5 StartZ=0 EndX=7.25 EndY=4.5 EndZ=0
    g7: LineSegment StartX=7.25 StartY=4.5 StartZ=0 EndX=7.25 EndY=7.3 EndZ=0
    g8: LineSegment StartX=7.25 StartY=-4.5 StartZ=0 EndX=7.75 EndY=-4.5 EndZ=0
    g9: LineSegment StartX=7.75 StartY=-4.5 StartZ=0 EndX=7.75 EndY=-7.3 EndZ=0
    g10: LineSegment StartX=7.75 StartY=-7.3 StartZ=0 EndX=7.25 EndY=-7.3 EndZ=0
    g11: LineSegment StartX=7.25 StartY=-7.3 StartZ=0 EndX=7.25 EndY=-4.5 EndZ=0
    g12: LineSegment StartX=-7.75 StartY=-4.5 StartZ=0 EndX=-7.25 EndY=-4.5 EndZ=0
    g13: LineSegment StartX=-7.25 StartY=-4.5 StartZ=0 EndX=-7.25 EndY=-7.3 EndZ=0
    g14: LineSegment StartX=-7.25 StartY=-7.3 StartZ=0 EndX=-7.75 EndY=-7.3 EndZ=0
    g15: LineSegment StartX=-7.75 StartY=-7.3 StartZ=0 EndX=-7.75 EndY=-4.5 EndZ=0
  constraints (46):
    c: Coincident(g0,g1)
    c: Coincident(g1,g2)
    c: Coincident(g2,g3)
    c: Coincident(g3,g0)
    c: Horizontal(g0)
    c: Horizontal(g2)
    c: Vertical(g1)
    c: Vertical(g3)
    c: DistanceX(g1,g-1) = 7.25
    c: DistanceX(g0,g0) = 0.5
    c: DistanceY(g3,g3) = 2.8
    c: DistanceY(g2) = 4.5
    c: Coincident(g4,g5)
    c: Coincident(g5,g6)
    c: Coincident(g6,g7)
    c: Coincident(g7,g4)
    c: Horizontal(g4)
    c: Horizontal(g6)
    c: Vertical(g5)
    c: Vertical(g7)
    c: Coincident(g8,g9)
    c: Coincident(g9,g10)
    c: Coincident(g10,g11)
    c: Coincident(g11,g8)
    c: Horizontal(g8)
    c: Horizontal(g10)
    c: Vertical(g9)
    c: Vertical(g11)
    c: Coincident(g12,g13)
    c: Coincident(g13,g14)
    c: Coincident(g14,g15)
    c: Coincident(g15,g12)
    c: Horizontal(g12)
    c: Horizontal(g14)
    c: Vertical(g13)
    c: Vertical(g15)
    c: Equal(g12,g8)
    c: Equal(g8,g6)
    c: Equal(g6,g2)
    c: Equal(g1,g7)
    c: Equal(g7,g11)
    c: Equal(g11,g13)
    c: Horizontal(g13,g10)
    c: Vertical(g8,g5)
    c: Symmetric(g0,g4,g-2)
    c: Symmetric(g12,g1,g-1)
FEATURE [PartDesign::Pad] Pad075
  AddSubType = 0
  AlongSketchNormal = false
  AutoTaperInnerAngle = true
  CheckUpToFaceLimits = true
  ClaimChildren = false
  Direction = (0,0,-1)
  Fit = 0
  FitJoin = 0
  FixShape = 1
  InnerFit = 0
  InnerFitJoin = 0
  InvalidShape = false
  Length = 8.5
  Length2 = 100
  NewSolid = false
  Placement = pos=(0,-4e-15,-19) rot=(1,0,0;3.14159rad)
  Profile = -> Sketch174
  ReferenceAxis = -> Sketch174 [N_Axis]
  Refine = true
  Suppress = false
  TaperInnerAngle = 0
  TaperInnerAngleRev = 0
  TreeRank = 0
  Type = 0
  ValidateShape = true
  _ProfileBasedVersion = 0
FEATURE [PartDesign::Chamfer] Chamfer045
  AddSubType = 0
  Angle = 45
  Base = -> Pad075 [Edge57,Edge53,Edge41,Edge37,Edge65,Edge61,Edge49,Edge45]
  BaseFeature = -> Pad075
  ChamferType = 0
  FixShape = 1
  FlipDirection = false
  InvalidShape = false
  NewSolid = false
  Placement = pos=(0,-4e-15,-19) rot=(1,0,0;3.14159rad)
  Refine = true
  Size = 0.6
  Size2 = 1
  SupportTransform = false
  Suppress = false
  TreeRank = 0
  UseAllEdges = false
  ValidateShape = true
FEATURE [Sketcher::SketchObject] Sketch175
  ArcFitTolerance = 0
  ExternalBSplineMaxDegree = 0
  ExternalBSplineTolerance = 0
  FixShape = 1
  FullyConstrained = false
  InternalTolerance = 1e-06
  InvalidShape = false
  MakeInternals = false
  MapMode = 5
  Placement = pos=(0,0,0) rot=(0.57735,0.57735,0.57735;2.0944rad)
  TreeRank = 0
  ValidateShape = false
  sketch-geometry (8):
    g0: ArcOfCircle CenterX=-6 CenterY=-38.7066 CenterZ=0 NormalX=0 NormalY=0 NormalZ=1 AngleXU=0 Radius=0.456793 StartAngle=1.3e-15 EndAngle=3.14159
    g1: ArcOfCircle CenterX=-6 CenterY=-40.4194 CenterZ=0 NormalX=0 NormalY=0 NormalZ=1 AngleXU=0 Radius=0.456793 StartAngle=3.14159 EndAngle=6.28319
    g2: LineSegment StartX=-6.45679 StartY=-38.7066 StartZ=0 EndX=-6.45679 EndY=-40.4194 EndZ=0
    g3: LineSegment StartX=-5.54321 StartY=-40.4194 StartZ=0 EndX=-5.54321 EndY=-38.7066 EndZ=0
    g4: ArcOfCircle CenterX=6 CenterY=-38.7066 CenterZ=0 NormalX=0 NormalY=0 NormalZ=1 AngleXU=0 Radius=0.417287 StartAngle=-5.3e-15 EndAngle=3.14159
    g5: ArcOfCircle CenterX=6 CenterY=-40.4194 CenterZ=0 NormalX=0 NormalY=0 NormalZ=1 AngleXU=0 Radius=0.417287 StartAngle=3.14159 EndAngle=6.28319
    g6: LineSegment StartX=5.58271 StartY=-38.7066 StartZ=0 EndX=5.58271 EndY=-40.4194 EndZ=0
    g7: LineSegment StartX=6.41729 StartY=-40.4194 StartZ=0 EndX=6.41729 EndY=-38.7066 EndZ=0
  constraints (14):
    c: Tangent(g0,g2) = -1.5708
    c: Tangent(g2,g1) = -1.5708
    c: Tangent(g1,g3) = -1.5708
    c: Tangent(g3,g0) = -1.5708
    c: Equal(g0,g1)
    c: Tangent(g4,g6) = -1.5708
    c: Tangent(g6,g5) = -1.5708
    c: Tangent(g5,g7) = -1.5708
    c: Tangent(g7,g4) = -1.5708
    c: Equal(g4,g5)
    c: Symmetric(g4,g0,g-2)
    c: Symmetric(g5,g1,g-2)
    c: Vertical(g1,g0)
    c: DistanceX(g0) = -6
FEATURE [PartDesign::Pocket] Pocket054
  AddSubType = 1
  AutoTaperInnerAngle = true
  BaseFeature = -> Chamfer045
  CheckUpToFaceLimits = true
  ClaimChildren = false
  Direction = (-1,-1e-16,1e-16)
  Fit = 0
  FitJoin = 0
  FixShape = 1
  InnerFit = 0
  InnerFitJoin = 0
  InvalidShape = false
  Length = 5
  Length2 = 100
  Midplane = true
  NewSolid = false
  Placement = pos=(0,-4e-15,-19) rot=(1,0,0;3.14159rad)
  Profile = -> Sketch175
  Refine = true
  Suppress = false
  TaperInnerAngle = 0
  TaperInnerAngleRev = 0
  TreeRank = 0
  Type = 1
  ValidateShape = true
  _ProfileBasedVersion = 0
  _Version = 0
FEATURE [PartDesign::Body] Body084  label="ElectronicPins"
  AutoGroupSolids = false
  ClaimAllChildren = false
  ExportMode = 0
  FixShape = 1
  Group = -> [Sketch174,Pad075,Chamfer045,Sketch175,Pocket054]
  InvalidShape = false
  Origin = -> Origin171
  SingleSolid = true
  Tip = -> Pocket054
  TreeRank = 0
  ValidateShape = false
  _ExportChildren = -> [Pad075,Chamfer045,Pocket054]
  _GroupVersion = 1
FEATURE [Sketcher::SketchObject] Sketch176
  ArcFitTolerance = 0
  ExternalBSplineMaxDegree = 0
  ExternalBSplineTolerance = 0
  FixShape = 1
  FullyConstrained = true
  InternalTolerance = 1e-06
  InvalidShape = false
  MakeInternals = false
  MapMode = 5
  Placement = pos=(0,0,0) rot=(0.57735,0.57735,0.57735;2.0944rad)
  TreeRank = 0
  ValidateShape = false
  sketch-geometry (12):
    g0: LineSegment StartX=-7.5 StartY=0 StartZ=0 EndX=-7.5 EndY=17 EndZ=0
    g1: LineSegment StartX=-7.5 StartY=17 StartZ=0 EndX=-12 EndY=17 EndZ=0
    g2: LineSegment StartX=-12 StartY=17 StartZ=0 EndX=-12 EndY=20 EndZ=0
    g3: LineSegment [constr] StartX=-7.5 StartY=0 StartZ=0 EndX=7.5 EndY=0 EndZ=0
    g4: LineSegment [constr] StartX=7.5 StartY=0 StartZ=0 EndX=7.5 EndY=17 EndZ=0
    g5: LineSegment [constr] StartX=7.5 StartY=17 StartZ=0 EndX=12 EndY=17 EndZ=0
    g6: LineSegment [constr] StartX=12 StartY=17 StartZ=0 EndX=12 EndY=20 EndZ=0
    g7: ArcOfCircle [constr] CenterX=-1.51e-14 CenterY=-51.5 CenterZ=0 NormalX=0 NormalY=0 NormalZ=1 AngleXU=0 Radius=72.5 StartAngle=1.40451 EndAngle=1.73708
    g8: GeomPoint [constr] X=4.5e-15 Y=21 Z=0
    g9: LineSegment StartX=0 StartY=0 StartZ=0 EndX=4.5e-15 EndY=21 EndZ=0
    g10: LineSegment StartX=-7.5 StartY=0 StartZ=0 EndX=0 EndY=0 EndZ=0
    g11: ArcOfCircle CenterX=-1.51e-14 CenterY=-51.5 CenterZ=0 NormalX=0 NormalY=0 NormalZ=1 AngleXU=0 Radius=72.5 StartAngle=1.5708 EndAngle=1.73708
  constraints (31):
    c: PointOnObject(g0,g-1)
    c: Vertical(g0)
    c: Coincident(g0,g1)
    c: Horizontal(g1)
    c: Coincident(g1,g2)
    c: Coincident(g0,g3)
    c: Coincident(g3,g4)
    c: Vertical(g4)
    c: Coincident(g4,g5)
    c: Horizontal(g5)
    c: Coincident(g5,g6)
    c: Vertical(g6)
    c: Vertical(g2)
    c: Equal(g6,g2)
    c: Symmetric(g0,g3,g-1)
    c: Symmetric(g6,g2,g-2)
    c: DistanceX(g0,g4) = 15
    c: DistanceY(g4) = 17
    c: DistanceY(g2,g2) = 3
    c: DistanceX(g1,g5) = 24
    c: Coincident(g7,g2)
    c: Coincident(g7,g6)
    c: PointOnObject(g8,g-2)
    c: Coincident(g9,g-1)
    c: Coincident(g9,g8)
    c: Coincident(g10,g0)
    c: Coincident(g10,g9)
    c: Coincident(g11,g7)
    c: Coincident(g11,g9)
    c: Coincident(g11,g2)
    c: DistanceY(g9) = 21
FEATURE [PartDesign::Revolution] Revolution015
  AddSubType = 0
  Angle = 360
  Axis = (1e-16,-1e-16,1)
  Base = (0,0,0)
  ClaimChildren = false
  Fit = 0
  FitJoin = 0
  FixShape = 1
  InnerFit = 0
  InnerFitJoin = 0
  InvalidShape = false
  NewSolid = false
  Placement = pos=(0,0,0) rot=(0.57735,0.57735,0.57735;2.0944rad)
  Profile = -> Sketch176
  ReferenceAxis = -> Sketch176 [V_Axis]
  Refine = true
  Suppress = false
  TreeRank = 0
  ValidateShape = true
  _ProfileBasedVersion = 0
FEATURE [PartDesign::Fillet] Fillet043
  AddSubType = 0
  Base = -> Revolution015 [Edge6]
  BaseFeature = -> Revolution015
  FixShape = 1
  InvalidShape = false
  NewSolid = false
  Placement = pos=(0,0,0) rot=(0.57735,0.57735,0.57735;2.0944rad)
  Radius = 1
  Refine = true
  SupportTransform = false
  Suppress = false
  TreeRank = 0
  UseAllEdges = false
  ValidateShape = true
FEATURE [PartDesign::Body] Body085  label="ButtonCaps"
  AutoGroupSolids = false
  ClaimAllChildren = false
  ExportMode = 0
  FixShape = 1
  Group = -> [Sketch176,Revolution015,Fillet043]
  InvalidShape = false
  Origin = -> Origin172
  SingleSolid = true
  Tip = -> Fillet043
  TreeRank = 0
  ValidateShape = false
  _ExportChildren = -> [Revolution015,Fillet043]
  _GroupVersion = 1
COMPONENT P25 — recipe-attached ("623ZZ", modeled in this document).
Construction recipe (the document's own serialized feature program — sketch geometry with constraints, then the solid features built on it; lengths are millimeters unless a unit is written):

FEATURE [Sketcher::SketchObject] Sketch202
  ArcFitTolerance = 0
  ExternalBSplineMaxDegree = 0
  ExternalBSplineTolerance = 0
  FixShape = 1
  FullyConstrained = true
  InternalTolerance = 1e-06
  InvalidShape = false
  MakeInternals = false
  MapMode = 5
  TreeRank = 0
  ValidateShape = false
  sketch-geometry (12):
    g0: LineSegment StartX=0 StartY=1.5 StartZ=0 EndX=4 EndY=1.5 EndZ=0
    g1: LineSegment StartX=4 StartY=1.5 StartZ=0 EndX=4 EndY=2.5 EndZ=0
    g2: LineSegment StartX=4 StartY=2.5 StartZ=0 EndX=3.5 EndY=2.5 EndZ=0
    g3: LineSegment StartX=3.5 StartY=2.5 StartZ=0 EndX=3.5 EndY=4 EndZ=0
    g4: LineSegment StartX=3.5 StartY=4 StartZ=0 EndX=4 EndY=4 EndZ=0
    g5: LineSegment StartX=4 StartY=4 StartZ=0 EndX=4 EndY=5 EndZ=0
    g6: LineSegment StartX=4 StartY=5 StartZ=0 EndX=0 EndY=5 EndZ=0
    g7: LineSegment StartX=0 StartY=5 StartZ=0 EndX=0 EndY=4 EndZ=0
    g8: LineSegment StartX=0 StartY=4 StartZ=0 EndX=0.5 EndY=4 EndZ=0
    g9: LineSegment StartX=0.5 StartY=4 StartZ=0 EndX=0.5 EndY=2.5 EndZ=0
    g10: LineSegment StartX=0.5 StartY=2.5 StartZ=0 EndX=0 EndY=2.5 EndZ=0
    g11: LineSegment StartX=0 StartY=2.5 StartZ=0 EndX=0 EndY=1.5 EndZ=0
  constraints (36):
    c: PointOnObject(g0,g-2)
    c: Horizontal(g0)
    c: Coincident(g1,g0)
    c: Vertical(g1)
    c: Coincident(g1,g2)
    c: Horizontal(g2)
    c: Coincident(g2,g3)
    c: Vertical(g3)
    c: Coincident(g3,g4)
    c: Horizontal(g4)
    c: Coincident(g4,g5)
    c: Vertical(g5)
    c: Coincident(g5,g6)
    c: PointOnObject(g6,g-2)
    c: Horizontal(g6)
    c: Coincident(g6,g7)
    c: PointOnObject(g7,g-2)
    c: Coincident(g7,g8)
    c: Horizontal(g8)
    c: Coincident(g8,g9)
    c: Vertical(g9)
    c: Coincident(g9,g10)
    c: PointOnObject(g10,g-2)
    c: Horizontal(g10)
    c: Coincident(g10,g11)
    c: Coincident(g11,g0)
    c: Equal(g4,g8)
    c: Equal(g10,g2)
    c: DistanceY(g-1,g0) = 1.5
    c: PointOnObject(g9,g2)
    c: PointOnObject(g8,g4)
    c: DistanceY(g-1,g6) = 5
    c: DistanceY(g-1,g10) = 2.5
    c: DistanceY(g-1,g7) = 4
    c: DistanceX(g6,g6) = 4
    c: DistanceX(g8,g3) = 3
FEATURE [PartDesign::Revolution] Revolution018
  AddSubType = 0
  Angle = 360
  Axis = (1,0,0)
  Base = (0,0,0)
  ClaimChildren = false
  Fit = 0
  FitJoin = 0
  FixShape = 1
  InnerFit = 0
  InnerFitJoin = 0
  InvalidShape = false
  NewSolid = false
  Profile = -> Sketch202
  ReferenceAxis = -> Sketch202 [H_Axis]
  Refine = true
  Suppress = false
  TreeRank = 0
  ValidateShape = true
  _ProfileBasedVersion = 0
FEATURE [PartDesign::Body] Body097
  AutoGroupSolids = false
  ClaimAllChildren = false
  ExportMode = 0
  FixShape = 1
  Group = -> [Sketch202,Revolution018]
  InvalidShape = false
  Origin = -> Origin188
  SingleSolid = true
  Tip = -> Revolution018
  TreeRank = 0
  ValidateShape = false
  _ExportChildren = -> [Revolution018]
  _GroupVersion = 1
FEATURE [Sketcher::SketchObject] Sketch203
  ArcFitTolerance = 0
  ExternalBSplineMaxDegree = 0
  ExternalBSplineTolerance = 0
  FixShape = 1
  FullyConstrained = true
  InternalTolerance = 1e-06
  InvalidShape = false
  MakeInternals = false
  MapMode = 5
  TreeRank = 0
  ValidateShape = false
  sketch-geometry (4):
    g0: LineSegment StartX=0.1 StartY=4 StartZ=0 EndX=3.9 EndY=4 EndZ=0
    g1: LineSegment StartX=3.9 StartY=4 StartZ=0 EndX=3.9 EndY=2.5 EndZ=0
    g2: LineSegment StartX=3.9 StartY=2.5 StartZ=0 EndX=0.1 EndY=2.5 EndZ=0
    g3: LineSegment StartX=0.1 StartY=2.5 StartZ=0 EndX=0.1 EndY=4 EndZ=0
  constraints (12):
    c: Coincident(g0,g1)
    c: Coincident(g1,g2)
    c: Coincident(g2,g3)
    c: Coincident(g3,g0)
    c: Horizontal(g0)
    c: Horizontal(g2)
    c: Vertical(g1)
    c: Vertical(g3)
    c: DistanceY(g-1,g2) = 2.5
    c: DistanceY(g-1,g0) = 4
    c: DistanceX(g0,g0) = 3.8
    c: DistanceX(g-1,g2) = 0.1
FEATURE [PartDesign::Revolution] Revolution019
  AddSubType = 0
  Angle = 360
  Axis = (1,0,0)
  Base = (0,0,0)
  ClaimChildren = false
  Fit = 0
  FitJoin = 0
  FixShape = 1
  InnerFit = 0
  InnerFitJoin = 0
  InvalidShape = false
  NewSolid = false
  Profile = -> Sketch203
  ReferenceAxis = -> Sketch203 [H_Axis]
  Refine = true
  Suppress = false
  TreeRank = 0
  ValidateShape = true
  _ProfileBasedVersion = 0
FEATURE [PartDesign::Body] Body098
  AutoGroupSolids = false
  ClaimAllChildren = false
  ExportMode = 0
  FixShape = 1
  Group = -> [Sketch203,Revolution019]
  InvalidShape = false
  Origin = -> Origin189
  SingleSolid = true
  Tip = -> Revolution019
  TreeRank = 0
  ValidateShape = false
  _ExportChildren = -> [Revolution019]
  _GroupVersion = 1
COMPONENT P26 — recipe-attached ("V623ZZ", modeled in this document).
Construction recipe (the document's own serialized feature program — sketch geometry with constraints, then the solid features built on it; lengths are millimeters unless a unit is written):

FEATURE [Sketcher::SketchObject] Sketch204
  ArcFitTolerance = 0
  ExternalBSplineMaxDegree = 0
  ExternalBSplineTolerance = 0
  FixShape = 1
  FullyConstrained = true
  InternalTolerance = 1e-06
  InvalidShape = false
  MakeInternals = false
  MapMode = 5
  TreeRank = 0
  ValidateShape = false
  sketch-geometry (7):
    g0: LineSegment StartX=4 StartY=0 StartZ=0 EndX=4 EndY=4 EndZ=0
    g1: LineSegment StartX=4 StartY=4 StartZ=0 EndX=6 EndY=4 EndZ=0
    g2: LineSegment StartX=6 StartY=4 StartZ=0 EndX=6 EndY=3.25 EndZ=0
    g3: LineSegment StartX=6 StartY=3.25 StartZ=0 EndX=4.85 EndY=2 EndZ=0
    g4: LineSegment StartX=4.85 StartY=2 StartZ=0 EndX=6 EndY=0.75 EndZ=0
    g5: LineSegment StartX=6 StartY=0.75 StartZ=0 EndX=6 EndY=0 EndZ=0
    g6: LineSegment StartX=6 StartY=0 StartZ=0 EndX=4 EndY=0 EndZ=0
  constraints (21):
    c: PointOnObject(g0,g-1)
    c: Vertical(g0)
    c: Coincident(g0,g1)
    c: Horizontal(g1)
    c: Coincident(g1,g2)
    c: Vertical(g2)
    c: Coincident(g2,g3)
    c: Coincident(g3,g4)
    c: Coincident(g4,g5)
    c: PointOnObject(g5,g-1)
    c: Vertical(g5)
    c: Coincident(g5,g6)
    c: Coincident(g6,g0)
    c: DistanceX(g-1,g0) = 4
    c: Equal(g3,g4)
    c: Equal(g1,g6)
    c: Equal(g5,g2)
    c: DistanceX(g-1,g5) = 6
    c: DistanceX(g-1,g3) = 4.85
    c: DistanceY(g0,g0) = 4
    c: DistanceY(g4,g2) = 2.5
FEATURE [PartDesign::Revolution] Revolution020
  AddSubType = 0
  Angle = 360
  Axis = (0,1,0)
  Base = (0,0,0)
  ClaimChildren = false
  Fit = 0
  FitJoin = 0
  FixShape = 1
  InnerFit = 0
  InnerFitJoin = 0
  InvalidShape = false
  NewSolid = false
  Profile = -> Sketch204
  ReferenceAxis = -> Sketch204 [V_Axis]
  Refine = true
  Reversed = true
  Suppress = false
  TreeRank = 0
  ValidateShape = true
  _ProfileBasedVersion = 0
FEATURE [PartDesign::Body] Body101  label="V623ZZ-extern"
  AutoGroupSolids = false
  ClaimAllChildren = false
  ExportMode = 0
  FixShape = 1
  Group = -> [Sketch204,Revolution020]
  InvalidShape = false
  Origin = -> Origin194
  SingleSolid = true
  Tip = -> Revolution020
  TreeRank = 0
  ValidateShape = false
  _ExportChildren = -> [Revolution020]
  _GroupVersion = 1
FEATURE [Sketcher::SketchObject] Sketch205
  ArcFitTolerance = 0
  ExternalBSplineMaxDegree = 0
  ExternalBSplineTolerance = 0
  FixShape = 1
  FullyConstrained = true
  InternalTolerance = 1e-06
  InvalidShape = false
  MakeInternals = false
  MapMode = 5
  Placement = pos=(0,0,0) rot=(0.57735,0.57735,0.57735;2.0944rad)
  TreeRank = 0
  ValidateShape = false
  sketch-geometry (8):
    g0: LineSegment StartX=0.2 StartY=4 StartZ=0 EndX=0.2 EndY=2.1 EndZ=0
    g1: LineSegment StartX=0.2 StartY=2.1 StartZ=0 EndX=0 EndY=2.1 EndZ=0
    g2: LineSegment StartX=0 StartY=2.1 StartZ=0 EndX=0 EndY=1.5 EndZ=0
    g3: LineSegment StartX=0 StartY=1.5 StartZ=0 EndX=4 EndY=1.5 EndZ=0
    g4: LineSegment StartX=4 StartY=1.5 StartZ=0 EndX=4 EndY=2.1 EndZ=0
    g5: LineSegment StartX=4 StartY=2.1 StartZ=0 EndX=3.8 EndY=2.1 EndZ=0
    g6: LineSegment StartX=3.8 StartY=2.1 StartZ=0 EndX=3.8 EndY=4 EndZ=0
    g7: LineSegment StartX=3.8 StartY=4 StartZ=0 EndX=0.2 EndY=4 EndZ=0
  constraints (24):
    c: Vertical(g0)
    c: Coincident(g0,g1)
    c: PointOnObject(g1,g-2)
    c: Horizontal(g1)
    c: Coincident(g1,g2)
    c: PointOnObject(g2,g-2)
    c: Coincident(g2,g3)
    c: Horizontal(g3)
    c: Coincident(g3,g4)
    c: Coincident(g4,g5)
    c: Horizontal(g5)
    c: Coincident(g5,g6)
    c: Vertical(g6)
    c: Coincident(g6,g7)
    c: Coincident(g7,g0)
    c: Horizontal(g7)
    c: DistanceY(g-1,g0) = 4
    c: Equal(g1,g5)
    c: Equal(g4,g2)
    c: DistanceX(g3,g3) = 4
    c: Vertical(g4)
    c: DistanceY(g-1,g2) = 1.5
    c: DistanceY(g2,g2) = 0.6
    c: DistanceX(g1,g1) = 0.2
FEATURE [PartDesign::Revolution] Revolution021
  AddSubType = 0
  Angle = 360
  Axis = (1e-16,1,-1e-16)
  Base = (0,0,0)
  ClaimChildren = false
  Fit = 0
  FitJoin = 0
  FixShape = 1
  InnerFit = 0
  InnerFitJoin = 0
  InvalidShape = false
  NewSolid = false
  Placement = pos=(0,0,0) rot=(0.57735,0.57735,0.57735;2.0944rad)
  Profile = -> Sketch205
  ReferenceAxis = -> Y_Axis120
  Refine = true
  Suppress = false
  TreeRank = 0
  ValidateShape = true
  _ProfileBasedVersion = 0
FEATURE [PartDesign::Body] Body100  label="V623ZZ-intern"
  AutoGroupSolids = false
  ClaimAllChildren = false
  ExportMode = 0
  FixShape = 1
  Group = -> [Sketch205,Revolution021]
  InvalidShape = false
  Origin = -> Origin193
  SingleSolid = true
  Tip = -> Revolution021
  TreeRank = 0
  ValidateShape = false
  _ExportChildren = -> [Revolution021]
  _GroupVersion = 1
COMPONENT P27 — recipe-attached ("MG-SG90", modeled in this document).
Construction recipe (the document's own serialized feature program — sketch geometry with constraints, then the solid features built on it; lengths are millimeters unless a unit is written):

FEATURE [Sketcher::SketchObject] Sketch162
  ArcFitTolerance = 0
  ExternalBSplineMaxDegree = 0
  ExternalBSplineTolerance = 0
  FixShape = 1
  FullyConstrained = true
  InternalTolerance = 1e-06
  InvalidShape = false
  MakeInternals = false
  MapMode = 5
  TreeRank = 0
  ValidateShape = false
  sketch-geometry (12):
    g0: LineSegment StartX=-17 StartY=2.106e-12 StartZ=0 EndX=-21.7 EndY=5.127e-13 EndZ=0
    g1: LineSegment StartX=-21.7 StartY=5.127e-13 StartZ=0 EndX=-21.7 EndY=-2.4 EndZ=0
    g2: LineSegment StartX=-21.7 StartY=-2.4 StartZ=0 EndX=-17 EndY=-2.4 EndZ=0
    g3: LineSegment StartX=-17 StartY=-2.4 StartZ=0 EndX=-17 EndY=-6.8 EndZ=0
    g4: LineSegment StartX=-17 StartY=-6.8 StartZ=0 EndX=6 EndY=-6.8 EndZ=0
    g5: LineSegment StartX=6 StartY=-6.8 StartZ=0 EndX=6 EndY=-2.4 EndZ=0
    g6: LineSegment StartX=6 StartY=-2.4 StartZ=0 EndX=10.7 EndY=-2.4 EndZ=0
    g7: LineSegment StartX=10.7 StartY=-2.4 StartZ=0 EndX=10.7 EndY=1.124e-12 EndZ=0
    g8: LineSegment StartX=10.7 StartY=1.1239e-12 StartZ=0 EndX=6 EndY=-1.9734e-12 EndZ=0
    g9: LineSegment StartX=6 StartY=-1.9734e-12 StartZ=0 EndX=6 EndY=15.8 EndZ=0
    g10: LineSegment StartX=6 StartY=15.8 StartZ=0 EndX=-17 EndY=15.8 EndZ=0
    g11: LineSegment StartX=-17 StartY=15.8 StartZ=0 EndX=-17 EndY=2.1068e-12 EndZ=0
  constraints (36):
    c: PointOnObject(g0,g-1)
    c: PointOnObject(g0,g-1)
    c: Coincident(g0,g1)
    c: Vertical(g1)
    c: Coincident(g1,g2)
    c: Horizontal(g2)
    c: Coincident(g2,g3)
    c: Vertical(g3)
    c: Coincident(g3,g4)
    c: Horizontal(g4)
    c: Coincident(g4,g5)
    c: Vertical(g5)
    c: Coincident(g5,g6)
    c: Horizontal(g6)
    c: Coincident(g6,g7)
    c: PointOnObject(g7,g-1)
    c: Vertical(g7)
    c: Coincident(g7,g8)
    c: PointOnObject(g8,g-1)
    c: Coincident(g8,g9)
    c: Vertical(g9)
    c: Coincident(g9,g10)
    c: Horizontal(g10)
    c: Coincident(g10,g11)
    c: Coincident(g11,g0)
    c: Vertical(g11)
    c: Equal(g0,g2)
    c: Equal(g2,g6)
    c: Equal(g6,g8)
    c: DistanceX(g4) = 6
    c: DistanceX(g4,g4) = 23
    c: DistanceX(g1,g6) = 32.4
    c: DistanceY(g3,g3) = 4.4
    c: DistanceY(g1,g1) = 2.4
    c: Equal(g7,g1)
    c: DistanceY(g9,g9) = 15.8
FEATURE [PartDesign::Pad] Pad068
  AddSubType = 0
  AlongSketchNormal = false
  AutoTaperInnerAngle = true
  CheckUpToFaceLimits = true
  ClaimChildren = false
  Direction = (0,0,1)
  Fit = 0
  FitJoin = 0
  FixShape = 1
  InnerFit = 0
  InnerFitJoin = 0
  InvalidShape = false
  Length = 12
  Length2 = 100
  Midplane = true
  NewSolid = false
  Profile = -> Sketch162
  Refine = true
  Suppress = false
  TaperInnerAngle = 0
  TaperInnerAngleRev = 0
  TreeRank = 0
  Type = 0
  ValidateShape = true
  _ProfileBasedVersion = 0
FEATURE [Sketcher::SketchObject] Sketch163
  ArcFitTolerance = 0
  AttachmentSupport = -> [Pad068]
  ExternalBSplineMaxDegree = 0
  ExternalBSplineTolerance = 0
  FixShape = 1
  FullyConstrained = true
  InternalTolerance = 1e-06
  InvalidShape = false
  MakeInternals = false
  MapMode = 5
  Placement = pos=(0,-6.8,0) rot=(1,0,0;1.5708rad)
  Support = -> [Pad068]
  TreeRank = 0
  ValidateShape = false
  sketch-geometry (4):
    g0: ArcOfCircle CenterX=-5.554e-13 CenterY=-7.838e-13 CenterZ=0 NormalX=0 NormalY=0 NormalZ=1 AngleXU=0 Radius=6 StartAngle=3.57137 EndAngle=8.995
    g1: ArcOfCircle CenterX=-6 CenterY=4.736e-13 CenterZ=0 NormalX=0 NormalY=0 NormalZ=1 AngleXU=0 Radius=2.5 StartAngle=1.5708 EndAngle=4.71239
    g2: LineSegment StartX=-6 StartY=2.5 StartZ=0 EndX=-5.45436 EndY=2.5 EndZ=0
    g3: LineSegment StartX=-6 StartY=-2.5 StartZ=0 EndX=-5.45436 EndY=-2.5 EndZ=0
  constraints (11):
    c: Coincident(g0,g-1)
    c: PointOnObject(g1,g-1)
    c: Coincident(g2,g0)
    c: Coincident(g3,g0)
    c: Horizontal(g3)
    c: Horizontal(g2)
    c: Tangent(g2,g1) = 1.5708
    c: Tangent(g3,g1) = -1.5708
    c: Radius(g0) = 6
    c: DistanceY(g1,g1) = 5
    c: DistanceX(g1,g0) = 6
FEATURE [PartDesign::Pad] Pad069
  AddSubType = 0
  AlongSketchNormal = false
  AutoTaperInnerAngle = true
  BaseFeature = -> Pad068
  CheckUpToFaceLimits = true
  ClaimChildren = false
  Direction = (0,-1,2e-16)
  Fit = 0
  FitJoin = 0
  FixShape = 1
  InnerFit = 0
  InnerFitJoin = 0
  InvalidShape = false
  Length = 4
  Length2 = 100
  NewSolid = false
  Profile = -> Sketch163
  Refine = true
  Suppress = false
  TaperInnerAngle = 0
  TaperInnerAngleRev = 0
  TreeRank = 0
  Type = 0
  ValidateShape = true
  _ProfileBasedVersion = 0
FEATURE [Sketcher::SketchObject] Sketch164
  ArcFitTolerance = 0
  ExternalBSplineMaxDegree = 0
  ExternalBSplineTolerance = 0
  ExternalGeometry = -> [Pad069]
  FixShape = 1
  FullyConstrained = true
  InternalTolerance = 1e-06
  InvalidShape = false
  MakeInternals = false
  MapMode = 5
  Placement = pos=(0,0,0) rot=(1,0,0;1.5708rad)
  TreeRank = 0
  ValidateShape = false
  sketch-geometry (4):
    g0: Circle CenterX=-19.25 CenterY=-8.88e-14 CenterZ=0 NormalX=0 NormalY=0 NormalZ=1 AngleXU=0 Radius=1
    g1: Circle CenterX=8.25 CenterY=8.765e-12 CenterZ=0 NormalX=0 NormalY=0 NormalZ=1 AngleXU=0 Radius=1
    g2: LineSegment [constr] StartX=-21.7 StartY=-6 StartZ=0 EndX=10.7 EndY=6 EndZ=0
    g3: GeomPoint [constr] X=-5.5 Y=5.2304e-12 Z=0
  constraints (8):
    c: PointOnObject(g0,g-1)
    c: DistanceX(g0,g1) = 27.5
    c: Equal(g0,g1)
    c: Diameter(g0) = 2
    c: Coincident(g2,g-3)
    c: Coincident(g2,g-4)
    c: Symmetric(g-4,g-3,g3)
    c: Symmetric(g0,g1,g3)
FEATURE [PartDesign::Pocket] Pocket052
  AddSubType = 1
  AutoTaperInnerAngle = true
  BaseFeature = -> Pad069
  CheckUpToFaceLimits = true
  ClaimChildren = false
  Direction = (0,1,0)
  Fit = 0
  FitJoin = 0
  FixShape = 1
  InnerFit = 0
  InnerFitJoin = 0
  InvalidShape = false
  Length = 5
  Length2 = 100
  NewSolid = false
  Profile = -> Sketch164
  Refine = true
  Reversed = true
  Suppress = false
  TaperInnerAngle = 0
  TaperInnerAngleRev = 0
  TreeRank = 0
  Type = 1
  ValidateShape = true
  _ProfileBasedVersion = 0
  _Version = 0
FEATURE [PartDesign::Body] Body076  label="BodyServo90S"
  AutoGroupSolids = false
  ClaimAllChildren = false
  ExportMode = 0
  FixShape = 1
  Group = -> [Sketch162,Pad068,Sketch163,Pad069,Sketch164,Pocket052]
  InvalidShape = false
  Origin = -> Origin195
  SingleSolid = true
  Tip = -> Pocket052
  TreeRank = 0
  ValidateShape = false
  _ExportChildren = -> [Pad068,Pad069,Pocket052]
  _GroupVersion = 1
FEATURE [Sketcher::SketchObject] Sketch165
  ArcFitTolerance = 0
  ExternalBSplineMaxDegree = 0
  ExternalBSplineTolerance = 0
  FixShape = 1
  FullyConstrained = true
  InternalTolerance = 1e-06
  InvalidShape = false
  MakeInternals = false
  MapMode = 5
  Placement = pos=(0,-10.8,2e-15) rot=(1,0,0;1.5708rad)
  TreeRank = 0
  ValidateShape = false
  sketch-geometry (1):
    g0: Circle CenterX=0 CenterY=0 CenterZ=0 NormalX=0 NormalY=0 NormalZ=1 AngleXU=0 Radius=2.25
  constraints (2):
    c: Coincident(g0,g-1)
    c: Diameter(g0) = 4.5
FEATURE [PartDesign::Pad] Pad070
  AddSubType = 0
  AlongSketchNormal = false
  AutoTaperInnerAngle = true
  CheckUpToFaceLimits = true
  ClaimChildren = false
  Direction = (0,-1,0)
  Fit = 0
  FitJoin = 0
  FixShape = 1
  InnerFit = 0
  InnerFitJoin = 0
  InvalidShape = false
  Length = 2.4
  Length2 = 100
  NewSolid = false
  Placement = pos=(0,-10.8,2e-15) rot=(1,0,0;1.5708rad)
  Profile = -> Sketch165
  Refine = true
  Suppress = false
  TaperInnerAngle = 0
  TaperInnerAngleRev = 0
  TreeRank = 0
  Type = 0
  ValidateShape = true
  _ProfileBasedVersion = 0
FEATURE [PartDesign::Body] Body077  label="AxleServo90S"
  AutoGroupSolids = false
  ClaimAllChildren = false
  ExportMode = 0
  FixShape = 1
  Group = -> [Sketch165,Pad070]
  InvalidShape = false
  Origin = -> Origin197
  SingleSolid = true
  Tip = -> Pad070
  TreeRank = 0
  ValidateShape = false
  _ExportChildren = -> [Pad070]
  _GroupVersion = 1
FEATURE [Sketcher::SketchObject] Sketch166
  ArcFitTolerance = 0
  AttachmentSupport = -> [Pocket052]
  ExternalBSplineMaxDegree = 0
  ExternalBSplineTolerance = 0
  FixShape = 1
  FullyConstrained = true
  InternalTolerance = 1e-06
  InvalidShape = false
  MakeInternals = false
  MapMode = 5
  Placement = pos=(6,0,0) rot=(0.57735,0.57735,0.57735;2.0944rad)
  Support = -> [Pocket052]
  TreeRank = 0
  ValidateShape = false
  sketch-geometry (3):
    g0: Circle CenterX=10 CenterY=-9.4173e-12 CenterZ=0 NormalX=0 NormalY=0 NormalZ=1 AngleXU=0 Radius=0.5
    g1: Circle CenterX=10 CenterY=1 CenterZ=0 NormalX=0 NormalY=0 NormalZ=1 AngleXU=0 Radius=0.5
    g2: Circle CenterX=10 CenterY=-1 CenterZ=0 NormalX=0 NormalY=0 NormalZ=1 AngleXU=0 Radius=0.5
  constraints (9):
    c: PointOnObject(g0,g-1)
    c: Tangent(g1,g0)
    c: Tangent(g2,g0)
    c: Vertical(g2,g0)
    c: Vertical(g0,g1)
    c: Equal(g1,g0)
    c: Equal(g1,g2)
    c: Diameter(g1) = 1
    c: DistanceX(g0) = 10
FEATURE [PartDesign::Pad] Pad071
  AddSubType = 0
  AlongSketchNormal = false
  AutoTaperInnerAngle = true
  CheckUpToFaceLimits = true
  ClaimChildren = false
  Direction = (1,0,0)
  Fit = 0
  FitJoin = 0
  FixShape = 1
  InnerFit = 0
  InnerFitJoin = 0
  InvalidShape = false
  Length = 10
  Length2 = 100
  NewSolid = false
  Profile = -> Sketch166
  Refine = true
  Suppress = false
  TaperInnerAngle = 0
  TaperInnerAngleRev = 0
  TreeRank = 0
  Type = 0
  ValidateShape = true
  _ProfileBasedVersion = 0
FEATURE [PartDesign::Body] Body078  label="Cables001"
  AutoGroupSolids = false
  ClaimAllChildren = false
  ExportMode = 0
  FixShape = 1
  Group = -> [Sketch166,Pad071]
  InvalidShape = false
  Origin = -> Origin163
  SingleSolid = true
  Tip = -> Pad071
  TreeRank = 0
  ValidateShape = false
  _ExportChildren = -> [Pad071]
  _GroupVersion = 1
COMPONENT P28 — recipe-attached ("SparkFun OTOS - SEN-24904", modeled in this document).
Construction recipe (the document's own serialized feature program — sketch geometry with constraints, then the solid features built on it; lengths are millimeters unless a unit is written):

FEATURE [Sketcher::SketchObject] Sketch210
  ArcFitTolerance = 0
  ExternalBSplineMaxDegree = 0
  ExternalBSplineTolerance = 0
  FixShape = 1
  FullyConstrained = true
  InternalTolerance = 1e-06
  InvalidShape = false
  MakeInternals = false
  MapMode = 5
  TreeRank = 0
  ValidateShape = false
  sketch-geometry (14):
    g0: LineSegment StartX=-12.7 StartY=-12.7 StartZ=0 EndX=12.7 EndY=-12.7 EndZ=0
    g1: LineSegment StartX=12.7 StartY=-12.7 StartZ=0 EndX=12.7 EndY=12.7 EndZ=0
    g2: LineSegment StartX=12.7 StartY=12.7 StartZ=0 EndX=-12.7 EndY=12.7 EndZ=0
    g3: LineSegment StartX=-12.7 StartY=12.7 StartZ=0 EndX=-12.7 EndY=-12.7 EndZ=0
    g4: GeomPoint [constr] X=0 Y=0 Z=0
    g5: LineSegment [constr] StartX=-10.16 StartY=-10.16 StartZ=0 EndX=10.16 EndY=-10.16 EndZ=0
    g6: LineSegment [constr] StartX=10.16 StartY=-10.16 StartZ=0 EndX=10.16 EndY=10.16 EndZ=0
    g7: LineSegment [constr] StartX=10.16 StartY=10.16 StartZ=0 EndX=-10.16 EndY=10.16 EndZ=0
    g8: LineSegment [constr] StartX=-10.16 StartY=10.16 StartZ=0 EndX=-10.16 EndY=-10.16 EndZ=0
    g9: GeomPoint [constr] X=0 Y=0 Z=0
    g10: Circle CenterX=-10.16 CenterY=10.16 CenterZ=0 NormalX=0 NormalY=0 NormalZ=1 AngleXU=0 Radius=1.5
    g11: Circle CenterX=10.16 CenterY=10.16 CenterZ=0 NormalX=0 NormalY=0 NormalZ=1 AngleXU=0 Radius=1.5
    g12: Circle CenterX=10.16 CenterY=-10.16 CenterZ=0 NormalX=0 NormalY=0 NormalZ=1 AngleXU=0 Radius=1.5
    g13: Circle CenterX=-10.16 CenterY=-10.16 CenterZ=0 NormalX=0 NormalY=0 NormalZ=1 AngleXU=0 Radius=1.5
  constraints (32):
    c: Coincident(g0,g1)
    c: Coincident(g1,g2)
    c: Coincident(g2,g3)
    c: Coincident(g3,g0)
    c: Horizontal(g0)
    c: Horizontal(g2)
    c: Vertical(g1)
    c: Vertical(g3)
    c: Symmetric(g2,g0,g4)
    c: Coincident(g4,g-1)
    c: DistanceX(g2,g2) = 25.4
    c: Equal(g1,g2)
    c: Coincident(g5,g6)
    c: Coincident(g6,g7)
    c: Coincident(g7,g8)
    c: Coincident(g8,g5)
    c: Horizontal(g5)
    c: Horizontal(g7)
    c: Vertical(g6)
    c: Vertical(g8)
    c: Symmetric(g7,g5,g9)
    c: Coincident(g9,g4)
    c: Equal(g6,g7)
    c: DistanceX(g7,g7) = 20.32
    c: Coincident(g10,g7)
    c: Coincident(g11,g6)
    c: Coincident(g12,g5)
    c: Coincident(g13,g5)
    c: Equal(g11,g10)
    c: Equal(g10,g13)
    c: Equal(g13,g12)
    c: Diameter(g11) = 3
FEATURE [PartDesign::Pad] Pad085
  AddSubType = 0
  AutoTaperInnerAngle = true
  CheckUpToFaceLimits = true
  ClaimChildren = false
  Direction = (0,0,1)
  Fit = 0
  FitJoin = 0
  FixShape = 1
  InnerFit = 0
  InnerFitJoin = 0
  InvalidShape = false
  Length = 1.6
  Length2 = 10
  NewSolid = false
  Profile = -> Sketch210
  ReferenceAxis = -> Sketch210 [N_Axis]
  Refine = true
  Suppress = false
  TaperInnerAngle = 0
  TaperInnerAngleRev = 0
  TreeRank = 0
  Type = 0
  ValidateShape = true
  _ProfileBasedVersion = 0
FEATURE [PartDesign::Body] Body102  label="SimpleOTOS-SparkFun"
  AutoGroupSolids = false
  ClaimAllChildren = false
  ExportMode = 0
  FixShape = 1
  Group = -> [Sketch210,Pad085]
  InvalidShape = false
  Origin = -> Origin201
  SingleSolid = true
  Tip = -> Pad085
  TreeRank = 0
  ValidateShape = false
  _ExportChildren = -> [Pad085]
  _GroupVersion = 1
COMPONENT P29 — recipe-attached ("100_deg_Corners", modeled in this document).
Construction recipe (the document's own serialized feature program — sketch geometry with constraints, then the solid features built on it; lengths are millimeters unless a unit is written):

FEATURE [Sketcher::SketchObject] Sketch212
  ArcFitTolerance = 0
  ExternalBSplineMaxDegree = 0
  ExternalBSplineTolerance = 0
  FixShape = 1
  FullyConstrained = true
  InternalTolerance = 1e-06
  InvalidShape = false
  MakeInternals = false
  MapMode = 5
  Placement = pos=(0,0,0) rot=(0.57735,0.57735,0.57735;2.0944rad)
  TreeRank = 0
  ValidateShape = false
  sketch-geometry (5):
    g0: LineSegment StartX=-5 StartY=-5 StartZ=0 EndX=5 EndY=-5 EndZ=0
    g1: LineSegment StartX=5 StartY=-5 StartZ=0 EndX=5 EndY=5 EndZ=0
    g2: LineSegment StartX=5 StartY=5 StartZ=0 EndX=-5 EndY=5 EndZ=0
    g3: LineSegment StartX=-5 StartY=5 StartZ=0 EndX=-5 EndY=-5 EndZ=0
    g4: GeomPoint [constr] X=0 Y=0 Z=0
  constraints (12):
    c: Coincident(g0,g1)
    c: Coincident(g1,g2)
    c: Coincident(g2,g3)
    c: Coincident(g3,g0)
    c: Horizontal(g0)
    c: Horizontal(g2)
    c: Vertical(g1)
    c: Vertical(g3)
    c: Symmetric(g2,g0,g4)
    c: Coincident(g4,g-1)
    c: Equal(g2,g1)
    c: DistanceX(g2,g2) = 10
FEATURE [PartDesign::Pad] Pad087
  AddSubType = 0
  AutoTaperInnerAngle = true
  CheckUpToFaceLimits = true
  ClaimChildren = false
  Direction = (1,1e-16,-1e-16)
  Fit = 0
  FitJoin = 0
  FixShape = 1
  InnerFit = 0
  InnerFitJoin = 0
  InvalidShape = false
  Length = 10
  Length2 = 10
  Midplane = true
  NewSolid = false
  Placement = pos=(0,0,0) rot=(0.57735,0.57735,0.57735;2.0944rad)
  Profile = -> Sketch212
  ReferenceAxis = -> Sketch212 [N_Axis]
  Refine = true
  Suppress = false
  TaperInnerAngle = 0
  TaperInnerAngleRev = 0
  TreeRank = 0
  Type = 0
  ValidateShape = true
  _ProfileBasedVersion = 0
FEATURE [Sketcher::SketchObject] Sketch213
  ArcFitTolerance = 0
  ExternalBSplineMaxDegree = 0
  ExternalBSplineTolerance = 0
  FixShape = 1
  FullyConstrained = true
  InternalTolerance = 1e-06
  InvalidShape = false
  MakeInternals = false
  MapMode = 5
  Placement = pos=(0,0,0) rot=(0.57735,0.57735,0.57735;2.0944rad)
  TreeRank = 0
  ValidateShape = false
  sketch-geometry (1):
    g0: Circle CenterX=0 CenterY=0 CenterZ=0 NormalX=0 NormalY=0 NormalZ=1 AngleXU=0 Radius=1.5
  constraints (2):
    c: Coincident(g0,g-1)
    c: Diameter(g0) = 3
FEATURE [PartDesign::Pocket] Pocket063
  AddSubType = 1
  AutoTaperInnerAngle = true
  BaseFeature = -> Pad087
  CheckUpToFaceLimits = true
  ClaimChildren = false
  Direction = (-1,-1e-16,1e-16)
  Fit = 0
  FitJoin = 0
  FixShape = 1
  InnerFit = 0
  InnerFitJoin = 0
  InvalidShape = false
  Length = 5
  Length2 = 5
  Midplane = true
  NewSolid = false
  Placement = pos=(0,0,0) rot=(0.57735,0.57735,0.57735;2.0944rad)
  Profile = -> Sketch213
  ReferenceAxis = -> Sketch213 [N_Axis]
  Refine = true
  Suppress = false
  TaperInnerAngle = 0
  TaperInnerAngleRev = 0
  TreeRank = 0
  Type = 1
  ValidateShape = true
  _ProfileBasedVersion = 0
  _Version = 0
FEATURE [PartDesign::PolarPattern] PolarPattern022
  AddSubType = 0
  Angle = 90
  Axis = -> Z_Axis126
  BaseFeature = -> Pocket063
  CopyShape = true
  FixShape = 1
  InvalidShape = false
  NewSolid = false
  Occurrences = 2
  OriginalSubs = -> [Pocket063]
  Originals = -> [Pocket063]
  ParallelTransform = true
  Placement = pos=(0,0,0) rot=(0.57735,0.57735,0.57735;2.0944rad)
  Refine = true
  SubTransform = true
  Suppress = false
  TreeRank = 0
  ValidateShape = true
  _Version = 0
FEATURE [Sketcher::SketchObject] Sketch214
  ArcFitTolerance = 0
  AttachmentSupport = -> [PolarPattern022]
  ExternalBSplineMaxDegree = 0
  ExternalBSplineTolerance = 0
  FixShape = 1
  FullyConstrained = true
  InternalTolerance = 1e-06
  InvalidShape = false
  MakeInternals = false
  MapMode = 5
  Placement = pos=(5,6.7e-15,-1.7e-15) rot=(0.57735,0.57735,0.57735;2.0944rad)
  Support = -> [PolarPattern022]
  TreeRank = 0
  ValidateShape = false
  sketch-geometry (1):
    g0: Circle CenterX=0 CenterY=0 CenterZ=0 NormalX=0 NormalY=0 NormalZ=1 AngleXU=0 Radius=3
  constraints (2):
    c: Coincident(g0,g-1)
    c: Diameter(g0) = 6
FEATURE [PartDesign::Pocket] Pocket064
  AddSubType = 1
  AutoTaperInnerAngle = true
  BaseFeature = -> PolarPattern022
  CheckUpToFaceLimits = true
  ClaimChildren = false
  Direction = (-1,-1.3e-15,2e-16)
  Fit = 0
  FitJoin = 0
  FixShape = 1
  InnerFit = 0
  InnerFitJoin = 0
  InvalidShape = false
  Length = 8
  Length2 = 5
  NewSolid = false
  Placement = pos=(0,0,0) rot=(0.57735,0.57735,0.57735;2.0944rad)
  Profile = -> Sketch214
  ReferenceAxis = -> Sketch214 [N_Axis]
  Refine = true
  Suppress = false
  TaperInnerAngle = 0
  TaperInnerAngleRev = 0
  TreeRank = 0
  Type = 0
  ValidateShape = true
  _ProfileBasedVersion = 0
  _Version = 0
FEATURE [Sketcher::SketchObject] Sketch215
  ArcFitTolerance = 0
  AttachmentSupport = -> [Pocket064]
  ExternalBSplineMaxDegree = 0
  ExternalBSplineTolerance = 0
  FixShape = 1
  FullyConstrained = true
  InternalTolerance = 1e-06
  InvalidShape = false
  MakeInternals = false
  MapMode = 5
  Placement = pos=(-6.7e-15,5,4.2e-15) rot=(-0.57735,-0.57735,-0.57735;2.0944rad)
  Support = -> [Pocket064]
  TreeRank = 0
  ValidateShape = false
  sketch-geometry (1):
    g0: Circle CenterX=0 CenterY=0 CenterZ=0 NormalX=0 NormalY=0 NormalZ=1 AngleXU=0 Radius=3
  constraints (2):
    c: Coincident(g0,g-1)
    c: Diameter(g0) = 6
FEATURE [PartDesign::Pocket] Pocket065
  AddSubType = 1
  AutoTaperInnerAngle = true
  BaseFeature = -> Pocket064
  CheckUpToFaceLimits = true
  ClaimChildren = false
  Direction = (1.3e-15,-1,-9e-16)
  Fit = 0
  FitJoin = 0
  FixShape = 1
  InnerFit = 0
  InnerFitJoin = 0
  InvalidShape = false
  Length = 8
  Length2 = 5
  NewSolid = false
  Placement = pos=(0,0,0) rot=(0.57735,0.57735,0.57735;2.0944rad)
  Profile = -> Sketch215
  ReferenceAxis = -> Sketch215 [N_Axis]
  Refine = true
  Suppress = false
  TaperInnerAngle = 0
  TaperInnerAngleRev = 0
  TreeRank = 0
  Type = 0
  ValidateShape = true
  _ProfileBasedVersion = 0
  _Version = 0
FEATURE [Sketcher::SketchObject] Sketch216
  ArcFitTolerance = 0
  ExternalBSplineMaxDegree = 0
  ExternalBSplineTolerance = 0
  ExternalGeometry = -> [Pocket065]
  FixShape = 1
  FullyConstrained = true
  InternalTolerance = 1e-06
  InvalidShape = false
  MakeInternals = false
  MapMode = 5
  Placement = pos=(0,0,0) rot=(0.57735,0.57735,0.57735;2.0944rad)
  TreeRank = 0
  ValidateShape = false
  sketch-geometry (3):
    g0: LineSegment StartX=-3 StartY=3 StartZ=0 EndX=-6 EndY=0 EndZ=0
    g1: LineSegment StartX=-3 StartY=1.43506e-08 StartZ=0 EndX=-6 EndY=0 EndZ=0
    g2: LineSegment StartX=-3 StartY=1.43506e-08 StartZ=0 EndX=-3 EndY=3 EndZ=0
  constraints (8):
    c: PointOnObject(g0,g-3)
    c: PointOnObject(g0,g-1)
    c: Coincident(g1,g-3)
    c: Coincident(g1,g0)
    c: Coincident(g2,g1)
    c: Coincident(g2,g0)
    c: DistanceY(g2,g2) = 3
    c: Angle(g0,g2) = 0.785398
FEATURE [PartDesign::Groove] Groove
  AddSubType = 1
  Angle = 360
  Axis = (1e-16,1,-1e-16)
  Base = (0,0,0)
  BaseFeature = -> Pocket065
  ClaimChildren = false
  Fit = 0
  FitJoin = 0
  FixShape = 1
  InnerFit = 0
  InnerFitJoin = 0
  InvalidShape = false
  NewSolid = false
  Placement = pos=(0,0,0) rot=(0.57735,0.57735,0.57735;2.0944rad)
  Profile = -> Sketch216
  ReferenceAxis = -> Y_Axis126
  Refine = true
  Reversed = true
  Suppress = false
  TreeRank = 0
  ValidateShape = true
  _ProfileBasedVersion = 0
FEATURE [PartDesign::PolarPattern] PolarPattern023
  AddSubType = 0
  Angle = 90
  Axis = -> Z_Axis126
  BaseFeature = -> Groove
  CopyShape = true
  FixShape = 1
  InvalidShape = false
  NewSolid = false
  Occurrences = 2
  OriginalSubs = -> [Groove]
  Originals = -> [Groove]
  ParallelTransform = true
  Placement = pos=(0,0,0) rot=(0.57735,0.57735,0.57735;2.0944rad)
  Refine = true
  Reversed = true
  SubTransform = true
  Suppress = false
  TreeRank = 0
  ValidateShape = true
  _Version = 0
FEATURE [Sketcher::SketchObject] Sketch217
  ArcFitTolerance = 0
  AttachmentSupport = -> [PolarPattern023]
  ExternalBSplineMaxDegree = 0
  ExternalBSplineTolerance = 0
  FixShape = 1
  FullyConstrained = true
  InternalTolerance = 1e-06
  InvalidShape = false
  MakeInternals = false
  MapMode = 5
  Placement = pos=(-2.5e-15,3e-15,-5) rot=(0.707107,0.707107,0;3.14159rad)
  Support = -> [PolarPattern023]
  TreeRank = 0
  ValidateShape = false
  sketch-geometry (1):
    g0: Circle CenterX=0 CenterY=0 CenterZ=0 NormalX=0 NormalY=0 NormalZ=1 AngleXU=0 Radius=3
  constraints (2):
    c: Coincident(g0,g-1)
    c: Diameter(g0) = 6
FEATURE [PartDesign::Pocket] Pocket066
  AddSubType = 1
  AutoTaperInnerAngle = true
  BaseFeature = -> PolarPattern023
  CheckUpToFaceLimits = true
  ClaimChildren = false
  Direction = (5e-16,-6e-16,1)
  Fit = 0
  FitJoin = 0
  FixShape = 1
  InnerFit = 0
  InnerFitJoin = 0
  InvalidShape = false
  Length = 5
  Length2 = 5
  NewSolid = false
  Placement = pos=(0,0,0) rot=(0.57735,0.57735,0.57735;2.0944rad)
  Profile = -> Sketch217
  ReferenceAxis = -> Sketch217 [N_Axis]
  Refine = true
  Suppress = false
  TaperInnerAngle = 0
  TaperInnerAngleRev = 0
  TreeRank = 0
  Type = 1
  ValidateShape = true
  _ProfileBasedVersion = 0
  _Version = 0
FEATURE [Sketcher::SketchObject] Sketch218
  ArcFitTolerance = 0
  ExternalBSplineMaxDegree = 0
  ExternalBSplineTolerance = 0
  ExternalGeometry = -> [Pocket066]
  FixShape = 1
  FullyConstrained = true
  InternalTolerance = 1e-06
  InvalidShape = false
  MakeInternals = false
  MapMode = 5
  Placement = pos=(0,0,0) rot=(0.57735,0.57735,0.57735;2.0944rad)
  TreeRank = 0
  ValidateShape = false
  sketch-geometry (5):
    g0: LineSegment StartX=-5 StartY=5 StartZ=0 EndX=-5.42979 EndY=7 EndZ=0
    g1: LineSegment StartX=-5.42979 StartY=7 StartZ=0 EndX=4.41829 EndY=8.73648 EndZ=0
    g2: LineSegment StartX=4.41829 StartY=8.73648 StartZ=0 EndX=5 EndY=5 EndZ=0
    g3: LineSegment StartX=5 StartY=5 StartZ=0 EndX=-5 EndY=5 EndZ=0
    g4: LineSegment [constr] StartX=2.1e-15 StartY=5 StartZ=0 EndX=-0.505748 EndY=7.86824 EndZ=0
  constraints (12):
    c: Coincident(g-3,g0)
    c: Coincident(g0,g1)
    c: Coincident(g1,g2)
    c: Coincident(g2,g-3)
    c: Coincident(g2,g3)
    c: Coincident(g3,g0)
    c: Distance(g1,g1) = 10
    c: Angle(g-2,g1) = 1.74533
    c: Symmetric(g3,g3,g4)
    c: Symmetric(g1,g1,g4)
    c: Perpendicular(g1,g4)
    c: DistanceY(g0,g0) = 2
FEATURE [PartDesign::Pad] Pad088
  AddSubType = 0
  AutoTaperInnerAngle = true
  BaseFeature = -> Pocket066
  CheckUpToFaceLimits = true
  ClaimChildren = false
  Direction = (1,1e-16,-1e-16)
  Fit = 0
  FitJoin = 0
  FixShape = 1
  InnerFit = 0
  InnerFitJoin = 0
  InvalidShape = false
  Length = 10
  Length2 = 10
  Midplane = true
  NewSolid = false
  Placement = pos=(0,0,0) rot=(0.57735,0.57735,0.57735;2.0944rad)
  Profile = -> Sketch218
  ReferenceAxis = -> Sketch218 [N_Axis]
  Refine = true
  Suppress = false
  TaperInnerAngle = 0
  TaperInnerAngleRev = 0
  TreeRank = 0
  Type = 0
  ValidateShape = true
  _ProfileBasedVersion = 0
FEATURE [Sketcher::SketchObject] Sketch219
  ArcFitTolerance = 0
  ExternalBSplineMaxDegree = 0
  ExternalBSplineTolerance = 0
  ExternalGeometry = -> [Pad088]
  FixShape = 1
  FullyConstrained = true
  InternalTolerance = 1e-06
  InvalidShape = false
  MakeInternals = false
  MapMode = 5
  Placement = pos=(0,0,0) rot=(0.57735,0.57735,0.57735;2.0944rad)
  TreeRank = 0
  ValidateShape = false
  sketch-geometry (8):
    g0: LineSegment [constr] StartX=-0.505748 StartY=7.86824 StartZ=0 EndX=-1.3e-15 EndY=5 EndZ=0
    g1: LineSegment StartX=-0.505748 StartY=7.86824 StartZ=0 EndX=0.971463 EndY=8.12871 EndZ=0
    g2: LineSegment StartX=0.971463 StartY=8.12871 StartZ=0 EndX=1.13419 EndY=7.20583 EndZ=0
    g3: LineSegment StartX=1.13419 StartY=7.20583 StartZ=0 EndX=2.81908 EndY=6.02606 EndZ=0
    g4: LineSegment StartX=2.81908 StartY=6.02606 StartZ=0 EndX=3 EndY=5 EndZ=0
    g5: LineSegment StartX=3 StartY=5 StartZ=0 EndX=0.0904611 EndY=4.48697 EndZ=0
    g6: LineSegment StartX=0.0904611 StartY=4.48697 StartZ=0 EndX=-0.505748 EndY=7.86824 EndZ=0
    g7: LineSegment [constr] StartX=-3 StartY=5 StartZ=0 EndX=2.81908 EndY=6.02606 EndZ=0
  constraints (20):
    c: Symmetric(g-4,g-4,g0)
    c: Symmetric(g-3,g-3,g0)
    c: Coincident(g0,g1)
    c: PointOnObject(g1,g-4)
    c: Coincident(g1,g2)
    c: Coincident(g2,g3)
    c: Coincident(g3,g4)
    c: Coincident(g4,g-3)
    c: Coincident(g4,g5)
    c: Coincident(g5,g6)
    c: Coincident(g6,g1)
    c: Perpendicular(g6,g5)
    c: Angle(g3,g5) = 0.785398
    c: Perpendicular(g1,g2)
    c: Distance(g1,g1) = 1.5
    c: PointOnObject(g0,g6)
    c: Perpendicular(g5,g4)
    c: Coincident(g7,g-3)
    c: Coincident(g7,g3)
    c: Perpendicular(g4,g7)
FEATURE [PartDesign::Line] DatumLine
  AttacherType = Attacher::AttachEngineLine
  AttachmentSupport = -> [Sketch219]
  FixShape = 1
  InvalidShape = false
  Length = 10
  MapMode = 24
  MinimumLength = 10
  Placement = pos=(1e-15,0.0904611,4.48697) rot=(0,0.996195,0.087156;3.14159rad)
  ResizeMode = 0
  Support = -> [Sketch219]
  TreeRank = 6
  ValidateShape = false
FEATURE [PartDesign::Groove] Groove004
  AddSubType = 1
  Angle = 360
  Axis = (-3e-16,0.173648,-0.984808)
  Base = (1e-15,0.0904611,4.48697)
  BaseFeature = -> Pad088
  ClaimChildren = false
  Fit = 0
  FitJoin = 0
  FixShape = 1
  InnerFit = 0
  InnerFitJoin = 0
  InvalidShape = false
  Linearize = true
  NewSolid = false
  Profile = -> Sketch219
  ReferenceAxis = -> DatumLine
  Refine = true
  Suppress = false
  TreeRank = 7
  ValidateShape = true
  _ProfileBasedVersion = 1
FEATURE [PartDesign::Body] Body104  label="Corner_100_deg"
  AutoGroupSolids = false
  ClaimAllChildren = false
  ExportMode = 0
  FixShape = 1
  Group = -> [Sketch212,Pad087,Sketch213,Pocket063,PolarPattern022,Sketch214,Pocket064,Sketch215,Pocket065,Sketch216,Groove,PolarPattern023,Sketch217,Pocket066,Sketch218,Pad088,DatumLine,Sketch219,Groove004]
  InvalidShape = false
  Origin = -> Origin203
  SingleSolid = true
  Tip = -> Groove004
  TreeRank = 0
  ValidateShape = false
  _ExportChildren = -> [Pad087,Pocket063,PolarPattern022,Pocket064,Pocket065,Groove,PolarPattern023,Pocket066,Pad088,DatumLine,Groove004]
  _GroupVersion = 1
FEATURE [PartDesign::FeatureBase] Clone
  BaseFeature = -> Body104
  FixShape = 1
  InvalidShape = false
  NewSolid = false
  Suppress = false
  TreeRank = 0
  ValidateShape = true
FEATURE [Sketcher::SketchObject] Sketch220
  ArcFitTolerance = 0
  AttachmentSupport = -> [Clone]
  ExternalBSplineMaxDegree = 0
  ExternalBSplineTolerance = 0
  ExternalGeometry = -> [Clone]
  FixShape = 1
  FullyConstrained = true
  InternalTolerance = 1e-06
  InvalidShape = false
  MakeInternals = false
  MapMode = 5
  Placement = pos=(5,6.7e-15,-2.2e-15) rot=(0.57735,0.57735,0.57735;2.0944rad)
  Support = -> [Clone]
  TreeRank = 0
  ValidateShape = false
  sketch-geometry (7):
    g0: LineSegment StartX=5 StartY=-5 StartZ=0 EndX=-15 EndY=-5 EndZ=0
    g1: LineSegment StartX=5 StartY=-5 StartZ=0 EndX=5 EndY=5 EndZ=0
    g2: LineSegment StartX=5 StartY=5 StartZ=0 EndX=3.44316 EndY=15 EndZ=0
    g3: LineSegment StartX=-15 StartY=-5 StartZ=0 EndX=-15 EndY=1.8e-15 EndZ=0
    g4: LineSegment StartX=3.44316 StartY=15 StartZ=0 EndX=9e-16 EndY=15 EndZ=0
    g5: ArcOfCircle CenterX=0 CenterY=0 CenterZ=0 NormalX=0 NormalY=0 NormalZ=1 AngleXU=0 Radius=15 StartAngle=1.5708 EndAngle=3.14159
    g6: Circle CenterX=0 CenterY=0 CenterZ=0 NormalX=0 NormalY=0 NormalZ=1 AngleXU=0 Radius=3
  constraints (18):
    c: Coincident(g0,g-5)
    c: Horizontal(g0)
    c: Coincident(g1,g0)
    c: Coincident(g1,g-4)
    c: Coincident(g2,g1)
    c: PointOnObject(g-3,g2)
    c: Coincident(g3,g0)
    c: PointOnObject(g3,g-1)
    c: Vertical(g3)
    c: Coincident(g4,g2)
    c: PointOnObject(g4,g-2)
    c: Horizontal(g4)
    c: Coincident(g5,g-1)
    c: Coincident(g5,g4)
    c: Coincident(g5,g3)
    c: DistanceX(g0,g0) = 20
    c: Coincident(g6,g5)
    c: Tangent(g6,g-6)
FEATURE [PartDesign::Pad] Pad089
  AddSubType = 0
  AutoTaperInnerAngle = true
  BaseFeature = -> Clone
  CheckUpToFaceLimits = true
  ClaimChildren = false
  Direction = (1,1.3e-15,-4e-16)
  Fit = 0
  FitJoin = 0
  FixShape = 1
  InnerFit = 0
  InnerFitJoin = 0
  InvalidShape = false
  Length = 3
  Length2 = 10
  NewSolid = false
  Profile = -> Sketch220
  ReferenceAxis = -> Sketch220 [N_Axis]
  Refine = true
  Suppress = false
  TaperInnerAngle = 0
  TaperInnerAngleRev = 0
  TreeRank = 0
  Type = 0
  ValidateShape = true
  _ProfileBasedVersion = 0
FEATURE [PartDesign::Chamfer] Chamfer054
  AddSubType = 0
  Angle = 45
  Base = -> Pad089 [Edge75,Edge85,Edge91,Edge26]
  BaseFeature = -> Pad089
  ChamferType = 0
  FixShape = 1
  FlipDirection = false
  InvalidShape = false
  NewSolid = false
  Refine = true
  Size = 1
  Size2 = 1
  SupportTransform = false
  Suppress = false
  TreeRank = 0
  UseAllEdges = false
  ValidateShape = true
FEATURE [PartDesign::Chamfer] Chamfer055
  AddSubType = 0
  Angle = 45
  Base = -> Chamfer054 [Face12]
  BaseFeature = -> Chamfer054
  ChamferType = 0
  FixShape = 1
  FlipDirection = false
  InvalidShape = false
  NewSolid = false
  Refine = true
  Size = 0.6
  Size2 = 1
  SupportTransform = false
  Suppress = false
  TreeRank = 0
  UseAllEdges = false
  ValidateShape = true
FEATURE [PartDesign::Body] Body105  label="Corner_100_deg_Side"
  AutoGroupSolids = false
  BaseFeature = -> Body104
  ClaimAllChildren = false
  ExportMode = 0
  FixShape = 1
  Group = -> [Clone,Sketch220,Pad089,Chamfer054,Chamfer055]
  InvalidShape = false
  Origin = -> Origin204
  SingleSolid = true
  Tip = -> Chamfer055
  TreeRank = 0
  ValidateShape = false
  _ExportChildren = -> [Clone,Pad089,Chamfer054,Chamfer055]
  _GroupVersion = 1
COMPONENT P30 — geometry summary ("100_deg_Corners_Mirror"; no construction recipe available for this part):
  bounding box: 20.0 x 20.0 x 13.0 mm
  tessellated surface: 5,192 triangles
  volume: 1675 mm^3 (32% of its bounding box)
COMPONENT P31 — recipe-attached ("MGN9C-RAIL", modeled in this document).
Construction recipe (the document's own serialized feature program — sketch geometry with constraints, then the solid features built on it; lengths are millimeters unless a unit is written):

FEATURE [PartDesign::FeatureBase] BaseFeature
  BaseFeature = -> Part__Feature002
  FixShape = 1
  InvalidShape = false
  NewSolid = false
  Suppress = false
  TreeRank = 0
  ValidateShape = true
FEATURE [PartDesign::Pad] Pad095
  AddSubType = 0
  AutoTaperInnerAngle = true
  BaseFeature = -> BaseFeature
  CheckUpToFaceLimits = true
  ClaimChildren = false
  Direction = (-1,0,0)
  Fit = 0
  FitJoin = 0
  FixShape = 1
  InnerFit = 0
  InnerFitJoin = 0
  InvalidShape = false
  Length = 125
  Length2 = 10
  NewSolid = false
  Profile = -> BaseFeature [Face20]
  Refine = true
  Suppress = false
  TaperInnerAngle = 0
  TaperInnerAngleRev = 0
  TreeRank = 0
  Type = 0
  ValidateShape = true
  _ProfileBasedVersion = 0
FEATURE [Sketcher::SketchObject] Sketch236
  ArcFitTolerance = 0
  ExternalBSplineMaxDegree = 0
  ExternalBSplineTolerance = 0
  ExternalGeometry = -> [Pad095]
  FixShape = 1
  FullyConstrained = false
  InternalTolerance = 1e-06
  InvalidShape = false
  MakeInternals = false
  MapMode = 5
  Placement = pos=(0,0,0) rot=(1,0,0;1.5708rad)
  TreeRank = 0
  ValidateShape = false
  sketch-geometry (1):
    g0: Circle CenterX=-7.5 CenterY=3e-16 CenterZ=0 NormalX=0 NormalY=0 NormalZ=1 AngleXU=0 Radius=1.75
  constraints (2):
    c: DistanceX(g-3,g-1) = 7.5
    c: DistanceX(g-4,g-3) = 20
FEATURE [PartDesign::Pocket] Pocket075
  AddSubType = 1
  AutoTaperInnerAngle = true
  BaseFeature = -> Pad095
  CheckUpToFaceLimits = true
  ClaimChildren = false
  Direction = (0,1,0)
  Fit = 0
  FitJoin = 0
  FixShape = 1
  InnerFit = 0
  InnerFitJoin = 0
  InvalidShape = false
  Length = 5
  Length2 = 5
  NewSolid = false
  Profile = -> Sketch236
  ReferenceAxis = -> Sketch236 [N_Axis]
  Refine = true
  Suppress = false
  TaperInnerAngle = 0
  TaperInnerAngleRev = 0
  TreeRank = 0
  Type = 1
  ValidateShape = true
  _ProfileBasedVersion = 0
  _Version = 0
FEATURE [PartDesign::LinearPattern] LinearPattern
  AddSubType = 0
  BaseFeature = -> Pocket075
  CopyShape = true
  Direction = -> X_Axis137
  FixShape = 1
  InvalidShape = false
  Length = 180
  NewSolid = false
  Occurrences = 10
  OriginalSubs = -> [Pocket075]
  Originals = -> [Pocket075]
  ParallelTransform = true
  Placement = pos=(-26.0308,-14.9133,0.499992) rot=(0,0,1;0rad)
  Refine = true
  Reversed = true
  SubTransform = true
  Suppress = false
  TreeRank = 0
  ValidateShape = true
  _Version = 0
FEATURE [PartDesign::Body] Body112  label="MGN9-200mm"
  AutoGroupSolids = false
  BaseFeature = -> Part__Feature002
  ClaimAllChildren = false
  ExportMode = 0
  FixShape = 1
  Group = -> [BaseFeature,Pad095,Sketch236,Pocket075,LinearPattern]
  InvalidShape = false
  Origin = -> Origin214
  SingleSolid = true
  Tip = -> LinearPattern
  TreeRank = 0
  ValidateShape = false
  _ExportChildren = -> [BaseFeature,Pad095,Pocket075,LinearPattern]
  _GroupVersion = 1
FEATURE [PartDesign::FeatureBase] Clone004
  BaseFeature = -> Body112
  FixShape = 1
  InvalidShape = false
  NewSolid = false
  Suppress = false
  TreeRank = 45
  ValidateShape = true
FEATURE [PartDesign::Pad] Pad099
  AddSubType = 0
  AlongSketchNormal = false
  AutoTaperInnerAngle = true
  BaseFeature = -> Clone004
  CheckUpToFaceLimits = true
  ClaimChildren = false
  Direction = (1,0,0)
  Fit = 0
  FitJoin = 0
  FixShape = 1
  InnerFit = 0
  InnerFitJoin = 0
  InvalidShape = false
  Length = 25
  Length2 = 10
  Linearize = true
  NewSolid = false
  Profile = -> Clone004 [Face19]
  Refine = true
  Suppress = false
  TaperInnerAngle = 0
  TaperInnerAngleRev = 0
  TreeRank = 47
  Type = 0
  ValidateShape = true
  _ProfileBasedVersion = 1
FEATURE [PartDesign::Body] Body115  label="MGN9-225mm-Custom"
  AutoGroupSolids = false
  BaseFeature = -> Body112
  ClaimAllChildren = false
  ExportMode = 0
  FixShape = 1
  Group = -> [Clone004,Pad099]
  InvalidShape = false
  Origin = -> Origin218
  SingleSolid = true
  Tip = -> Pad099
  TreeRank = 46
  ValidateShape = false
  _ExportChildren = -> [Clone004,Pad099]
  _GroupVersion = 1
